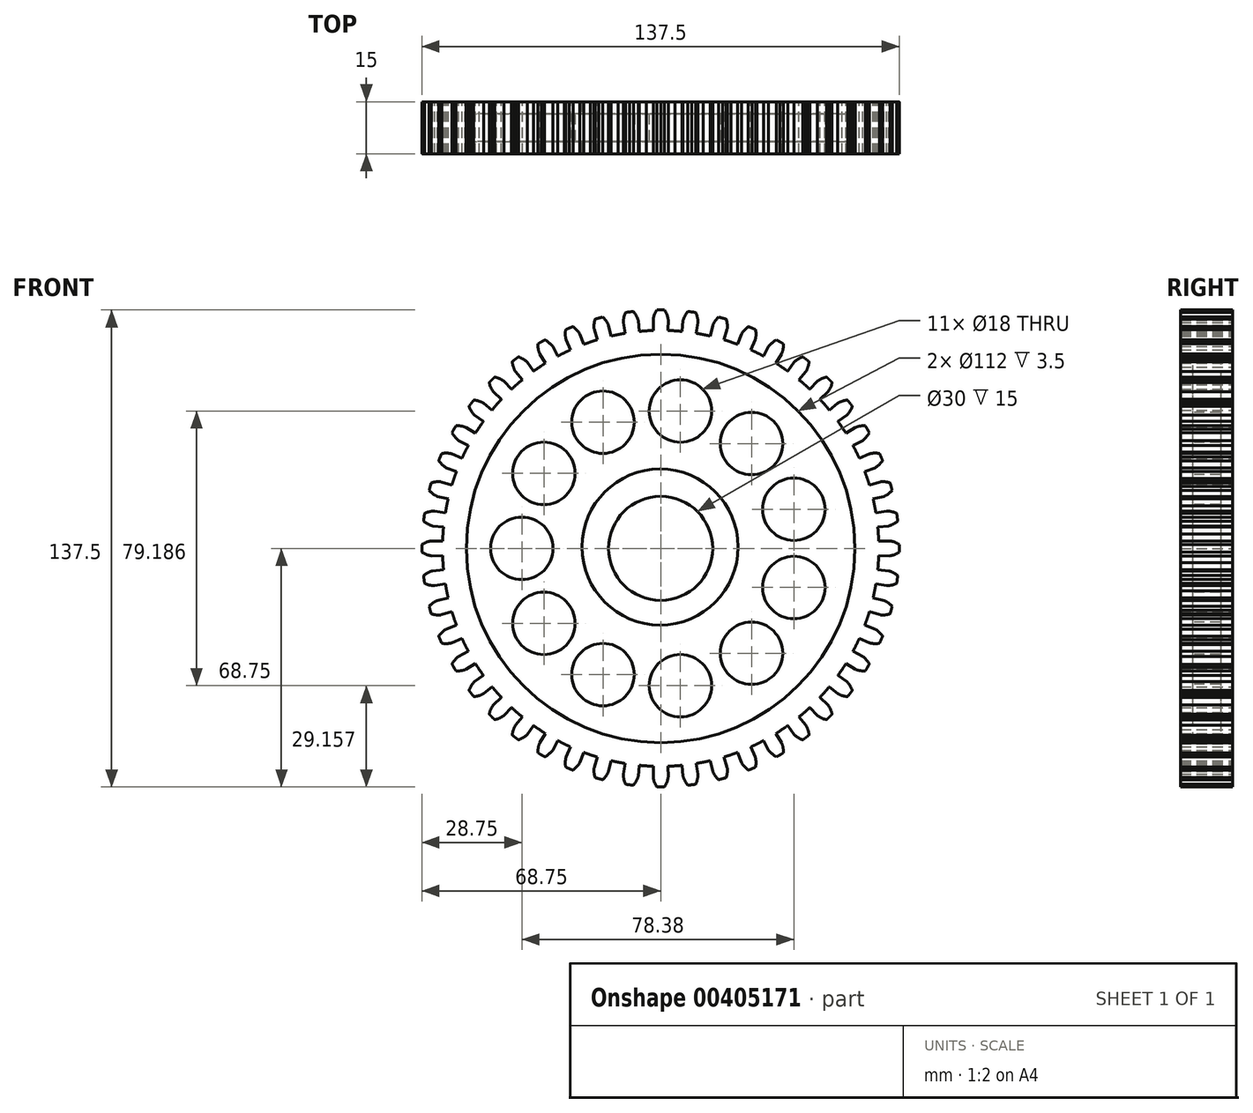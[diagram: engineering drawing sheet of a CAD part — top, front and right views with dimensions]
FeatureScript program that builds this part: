
annotation { "Feature Type Name" : "Feature", "Feature Type Description" : "" }
export const myFeature = defineFeature(function(context is Context, id is Id, definition is map)
    precondition{}
    {
        {
            var Q0;
            Q0=qCreatedBy(makeId("Front.planeOp"),FACE);
            var sketch = newSketch(context, id + "F0", { "sketchPlane" : qUnion([Q0])});
            skArc(sketch, "E0", {"start": v(68.74, -1.12) * mm, "mid": v(68.75, 0) * mm, "end": v(68.74, 1.12) * mm});
            skArc(sketch, "E1", {"start": v(62.82, 2.06) * mm, "mid": v(-62.85, 0) * mm, "end": v(62.82, -2.06) * mm});
            skLineSegment(sketch, "E2", {"start": v(62.82, 2.06) * mm, "end": v(65.96, 2.16) * mm});
            skLineSegment(sketch, "E3", {"start": v(62.82, 1.03) * mm, "end": v(62.84, 1.03) * mm});
            skArc(sketch, "E4", {"start": v(68.74, 1.12) * mm, "mid": v(67.41, 1.8) * mm, "end": v(65.96, 2.16) * mm});
            skLineSegment(sketch, "E5", {"start": v(65.96, 2.16) * mm, "end": v(62.82, 2.06) * mm});
            skArc(sketch, "E6", {"start": v(62.82, 2.06) * mm, "mid": v(62.78, 3.08) * mm, "end": v(62.72, 4.11) * mm});
            skArc(sketch, "E7", {"start": v(68.75, 0) * mm, "mid": v(68.75, 0.56) * mm, "end": v(68.74, 1.12) * mm});
            skLineSegment(sketch, "E8", {"start": v(62.78, 0) * mm, "end": v(62.85, 0) * mm});
            skArc(sketch, "E9.MirrorCS", {"start": v(68.75, 0) * mm, "mid": v(68.75, -0.56) * mm, "end": v(68.74, -1.12) * mm});
            skLineSegment(sketch, "E10.MirrorCS", {"start": v(65.96, -2.16) * mm, "end": v(62.82, -2.06) * mm});
            skArc(sketch, "E11.MirrorCS", {"start": v(68.74, -1.12) * mm, "mid": v(67.41, -1.8) * mm, "end": v(65.96, -2.16) * mm});
            skArc(sketch, "E12.MirrorCS", {"start": v(62.82, -2.06) * mm, "mid": v(62.78, -3.08) * mm, "end": v(62.72, -4.11) * mm});
            skPoint(sketch, "E13.trimOffspring.end.orphan", {"position": v(73.8, 0) * mm});
            skArc(sketch, "E14.1.0", {"start": v(62.01, 10.24) * mm, "mid": v(61.84, 11.25) * mm, "end": v(61.64, 12.26) * mm});
            skLineSegment(sketch, "E14.1.1", {"start": v(65.12, 10.75) * mm, "end": v(62.01, 10.24) * mm});
            skArc(sketch, "E14.1.2", {"start": v(68, 10.09) * mm, "mid": v(66.6, 10.59) * mm, "end": v(65.12, 10.75) * mm});
            skArc(sketch, "E14.1.3", {"start": v(68.16, 8.97) * mm, "mid": v(68.09, 9.53) * mm, "end": v(68, 10.09) * mm});
            skArc(sketch, "E14.1.4", {"start": v(68.16, 8.97) * mm, "mid": v(68.24, 8.42) * mm, "end": v(68.3, 7.86) * mm});
            skArc(sketch, "E14.1.5", {"start": v(68.3, 7.86) * mm, "mid": v(67.07, 7.01) * mm, "end": v(65.68, 6.47) * mm});
            skLineSegment(sketch, "E14.1.6", {"start": v(65.68, 6.47) * mm, "end": v(62.55, 6.16) * mm});
            skArc(sketch, "E14.1.7", {"start": v(62.55, 6.16) * mm, "mid": v(62.65, 5.14) * mm, "end": v(62.72, 4.11) * mm});
            skArc(sketch, "E14.2.0", {"start": v(60.14, 18.24) * mm, "mid": v(59.85, 19.23) * mm, "end": v(59.51, 20.2) * mm});
            skLineSegment(sketch, "E14.2.1", {"start": v(63.16, 19.16) * mm, "end": v(60.14, 18.24) * mm});
            skArc(sketch, "E14.2.2", {"start": v(66.1, 18.88) * mm, "mid": v(64.65, 19.19) * mm, "end": v(63.16, 19.16) * mm});
            skArc(sketch, "E14.2.3", {"start": v(66.4, 17.8) * mm, "mid": v(66.26, 18.34) * mm, "end": v(66.1, 18.88) * mm});
            skArc(sketch, "E14.2.4", {"start": v(66.4, 17.8) * mm, "mid": v(66.55, 17.25) * mm, "end": v(66.69, 16.7) * mm});
            skArc(sketch, "E14.2.5", {"start": v(66.69, 16.7) * mm, "mid": v(65.58, 15.7) * mm, "end": v(64.28, 14.99) * mm});
            skLineSegment(sketch, "E14.2.6", {"start": v(64.28, 14.99) * mm, "end": v(61.2, 14.27) * mm});
            skArc(sketch, "E14.2.7", {"start": v(61.2, 14.27) * mm, "mid": v(61.44, 13.27) * mm, "end": v(61.64, 12.26) * mm});
            skArc(sketch, "E14.3.0", {"start": v(57.25, 25.94) * mm, "mid": v(56.82, 26.88) * mm, "end": v(56.37, 27.8) * mm});
            skLineSegment(sketch, "E14.3.1", {"start": v(60.12, 27.24) * mm, "end": v(57.25, 25.94) * mm});
            skArc(sketch, "E14.3.2", {"start": v(63.08, 27.34) * mm, "mid": v(61.6, 27.46) * mm, "end": v(60.12, 27.24) * mm});
            skArc(sketch, "E14.3.3", {"start": v(63.52, 26.3) * mm, "mid": v(63.3, 26.83) * mm, "end": v(63.08, 27.34) * mm});
            skArc(sketch, "E14.3.4", {"start": v(63.52, 26.3) * mm, "mid": v(63.73, 25.8) * mm, "end": v(63.94, 25.27) * mm});
            skArc(sketch, "E14.3.5", {"start": v(63.94, 25.27) * mm, "mid": v(62.97, 24.13) * mm, "end": v(61.77, 23.25) * mm});
            skLineSegment(sketch, "E14.3.6", {"start": v(61.77, 23.25) * mm, "end": v(58.82, 22.14) * mm});
            skArc(sketch, "E14.3.7", {"start": v(58.82, 22.14) * mm, "mid": v(59.18, 21.18) * mm, "end": v(59.51, 20.2) * mm});
            skArc(sketch, "E14.4.0", {"start": v(53.37, 33.19) * mm, "mid": v(52.83, 34.06) * mm, "end": v(52.26, 34.92) * mm});
            skLineSegment(sketch, "E14.4.1", {"start": v(56.05, 34.85) * mm, "end": v(53.37, 33.19) * mm});
            skArc(sketch, "E14.4.2", {"start": v(58.97, 35.34) * mm, "mid": v(57.48, 35.27) * mm, "end": v(56.05, 34.85) * mm});
            skArc(sketch, "E14.4.3", {"start": v(59.54, 34.37) * mm, "mid": v(59.26, 34.86) * mm, "end": v(58.97, 35.34) * mm});
            skArc(sketch, "E14.4.4", {"start": v(59.54, 34.37) * mm, "mid": v(59.82, 33.89) * mm, "end": v(60.1, 33.4) * mm});
            skArc(sketch, "E14.4.5", {"start": v(60.1, 33.4) * mm, "mid": v(59.28, 32.14) * mm, "end": v(58.2, 31.11) * mm});
            skLineSegment(sketch, "E14.4.6", {"start": v(58.2, 31.11) * mm, "end": v(55.43, 29.63) * mm});
            skArc(sketch, "E14.4.7", {"start": v(55.43, 29.63) * mm, "mid": v(55.91, 28.72) * mm, "end": v(56.37, 27.8) * mm});
            skArc(sketch, "E14.5.0", {"start": v(48.58, 39.87) * mm, "mid": v(47.93, 40.67) * mm, "end": v(47.25, 41.44) * mm});
            skLineSegment(sketch, "E14.5.1", {"start": v(51.02, 41.87) * mm, "end": v(48.58, 39.87) * mm});
            skArc(sketch, "E14.5.2", {"start": v(53.85, 42.74) * mm, "mid": v(52.38, 42.47) * mm, "end": v(51.02, 41.87) * mm});
            skArc(sketch, "E14.5.3", {"start": v(54.54, 41.85) * mm, "mid": v(54.2, 42.3) * mm, "end": v(53.85, 42.74) * mm});
            skArc(sketch, "E14.5.4", {"start": v(54.54, 41.85) * mm, "mid": v(54.89, 41.4) * mm, "end": v(55.22, 40.95) * mm});
            skArc(sketch, "E14.5.5", {"start": v(55.22, 40.95) * mm, "mid": v(54.58, 39.6) * mm, "end": v(53.65, 38.44) * mm});
            skLineSegment(sketch, "E14.5.6", {"start": v(53.65, 38.44) * mm, "end": v(51.09, 36.6) * mm});
            skArc(sketch, "E14.5.7", {"start": v(51.09, 36.6) * mm, "mid": v(51.69, 35.77) * mm, "end": v(52.26, 34.92) * mm});
            skArc(sketch, "E14.6.0", {"start": v(42.96, 45.87) * mm, "mid": v(42.21, 46.58) * mm, "end": v(41.44, 47.25) * mm});
            skLineSegment(sketch, "E14.6.1", {"start": v(45.12, 48.17) * mm, "end": v(42.96, 45.87) * mm});
            skArc(sketch, "E14.6.2", {"start": v(47.81, 49.4) * mm, "mid": v(46.4, 48.94) * mm, "end": v(45.12, 48.17) * mm});
            skArc(sketch, "E14.6.3", {"start": v(48.61, 48.61) * mm, "mid": v(48.22, 49.01) * mm, "end": v(47.81, 49.4) * mm});
            skArc(sketch, "E14.6.4", {"start": v(48.61, 48.61) * mm, "mid": v(49.01, 48.22) * mm, "end": v(49.4, 47.81) * mm});
            skArc(sketch, "E14.6.5", {"start": v(49.4, 47.81) * mm, "mid": v(48.94, 46.4) * mm, "end": v(48.17, 45.12) * mm});
            skLineSegment(sketch, "E14.6.6", {"start": v(48.17, 45.12) * mm, "end": v(45.87, 42.96) * mm});
            skArc(sketch, "E14.6.7", {"start": v(45.87, 42.96) * mm, "mid": v(46.58, 42.21) * mm, "end": v(47.25, 41.44) * mm});
            skArc(sketch, "E14.7.0", {"start": v(36.6, 51.09) * mm, "mid": v(35.77, 51.69) * mm, "end": v(34.92, 52.26) * mm});
            skLineSegment(sketch, "E14.7.1", {"start": v(38.44, 53.65) * mm, "end": v(36.6, 51.09) * mm});
            skArc(sketch, "E14.7.2", {"start": v(40.95, 55.22) * mm, "mid": v(39.6, 54.58) * mm, "end": v(38.44, 53.65) * mm});
            skArc(sketch, "E14.7.3", {"start": v(41.85, 54.54) * mm, "mid": v(41.4, 54.89) * mm, "end": v(40.95, 55.22) * mm});
            skArc(sketch, "E14.7.4", {"start": v(41.85, 54.54) * mm, "mid": v(42.3, 54.2) * mm, "end": v(42.74, 53.85) * mm});
            skArc(sketch, "E14.7.5", {"start": v(42.74, 53.85) * mm, "mid": v(42.47, 52.38) * mm, "end": v(41.87, 51.02) * mm});
            skLineSegment(sketch, "E14.7.6", {"start": v(41.87, 51.02) * mm, "end": v(39.87, 48.58) * mm});
            skArc(sketch, "E14.7.7", {"start": v(39.87, 48.58) * mm, "mid": v(40.67, 47.93) * mm, "end": v(41.44, 47.25) * mm});
            skArc(sketch, "E14.8.0", {"start": v(29.63, 55.43) * mm, "mid": v(28.72, 55.91) * mm, "end": v(27.8, 56.37) * mm});
            skLineSegment(sketch, "E14.8.1", {"start": v(31.11, 58.2) * mm, "end": v(29.63, 55.43) * mm});
            skArc(sketch, "E14.8.2", {"start": v(33.4, 60.1) * mm, "mid": v(32.14, 59.28) * mm, "end": v(31.11, 58.2) * mm});
            skArc(sketch, "E14.8.3", {"start": v(34.37, 59.54) * mm, "mid": v(33.89, 59.82) * mm, "end": v(33.4, 60.1) * mm});
            skArc(sketch, "E14.8.4", {"start": v(34.37, 59.54) * mm, "mid": v(34.86, 59.26) * mm, "end": v(35.34, 58.97) * mm});
            skArc(sketch, "E14.8.5", {"start": v(35.34, 58.97) * mm, "mid": v(35.27, 57.48) * mm, "end": v(34.85, 56.05) * mm});
            skLineSegment(sketch, "E14.8.6", {"start": v(34.85, 56.05) * mm, "end": v(33.19, 53.37) * mm});
            skArc(sketch, "E14.8.7", {"start": v(33.19, 53.37) * mm, "mid": v(34.06, 52.83) * mm, "end": v(34.92, 52.26) * mm});
            skArc(sketch, "E14.9.0", {"start": v(22.14, 58.82) * mm, "mid": v(21.18, 59.18) * mm, "end": v(20.2, 59.51) * mm});
            skLineSegment(sketch, "E14.9.1", {"start": v(23.25, 61.77) * mm, "end": v(22.14, 58.82) * mm});
            skArc(sketch, "E14.9.2", {"start": v(25.27, 63.94) * mm, "mid": v(24.13, 62.97) * mm, "end": v(23.25, 61.77) * mm});
            skArc(sketch, "E14.9.3", {"start": v(26.3, 63.52) * mm, "mid": v(25.8, 63.73) * mm, "end": v(25.27, 63.94) * mm});
            skArc(sketch, "E14.9.4", {"start": v(26.3, 63.52) * mm, "mid": v(26.83, 63.3) * mm, "end": v(27.34, 63.08) * mm});
            skArc(sketch, "E14.9.5", {"start": v(27.34, 63.08) * mm, "mid": v(27.46, 61.6) * mm, "end": v(27.24, 60.12) * mm});
            skLineSegment(sketch, "E14.9.6", {"start": v(27.24, 60.12) * mm, "end": v(25.94, 57.25) * mm});
            skArc(sketch, "E14.9.7", {"start": v(25.94, 57.25) * mm, "mid": v(26.88, 56.82) * mm, "end": v(27.8, 56.37) * mm});
            skArc(sketch, "E14.10.0", {"start": v(14.27, 61.2) * mm, "mid": v(13.27, 61.44) * mm, "end": v(12.26, 61.64) * mm});
            skLineSegment(sketch, "E14.10.1", {"start": v(14.99, 64.28) * mm, "end": v(14.27, 61.2) * mm});
            skArc(sketch, "E14.10.2", {"start": v(16.7, 66.69) * mm, "mid": v(15.7, 65.58) * mm, "end": v(14.99, 64.28) * mm});
            skArc(sketch, "E14.10.3", {"start": v(17.8, 66.4) * mm, "mid": v(17.25, 66.55) * mm, "end": v(16.7, 66.69) * mm});
            skArc(sketch, "E14.10.4", {"start": v(17.8, 66.4) * mm, "mid": v(18.34, 66.26) * mm, "end": v(18.88, 66.1) * mm});
            skArc(sketch, "E14.10.5", {"start": v(18.88, 66.1) * mm, "mid": v(19.19, 64.65) * mm, "end": v(19.16, 63.16) * mm});
            skLineSegment(sketch, "E14.10.6", {"start": v(19.16, 63.16) * mm, "end": v(18.24, 60.14) * mm});
            skArc(sketch, "E14.10.7", {"start": v(18.24, 60.14) * mm, "mid": v(19.23, 59.85) * mm, "end": v(20.2, 59.51) * mm});
            skArc(sketch, "E14.11.0", {"start": v(6.16, 62.55) * mm, "mid": v(5.14, 62.65) * mm, "end": v(4.11, 62.72) * mm});
            skLineSegment(sketch, "E14.11.1", {"start": v(6.47, 65.68) * mm, "end": v(6.16, 62.55) * mm});
            skArc(sketch, "E14.11.2", {"start": v(7.86, 68.3) * mm, "mid": v(7.01, 67.07) * mm, "end": v(6.47, 65.68) * mm});
            skArc(sketch, "E14.11.3", {"start": v(8.97, 68.16) * mm, "mid": v(8.42, 68.24) * mm, "end": v(7.86, 68.3) * mm});
            skArc(sketch, "E14.11.4", {"start": v(8.97, 68.16) * mm, "mid": v(9.53, 68.09) * mm, "end": v(10.09, 68) * mm});
            skArc(sketch, "E14.11.5", {"start": v(10.09, 68) * mm, "mid": v(10.59, 66.6) * mm, "end": v(10.75, 65.12) * mm});
            skLineSegment(sketch, "E14.11.6", {"start": v(10.75, 65.12) * mm, "end": v(10.24, 62.01) * mm});
            skArc(sketch, "E14.11.7", {"start": v(10.24, 62.01) * mm, "mid": v(11.25, 61.84) * mm, "end": v(12.26, 61.64) * mm});
            skArc(sketch, "E14.12.0", {"start": v(-2.06, 62.82) * mm, "mid": v(-3.08, 62.78) * mm, "end": v(-4.11, 62.72) * mm});
            skLineSegment(sketch, "E14.12.1", {"start": v(-2.16, 65.96) * mm, "end": v(-2.06, 62.82) * mm});
            skArc(sketch, "E14.12.2", {"start": v(-1.12, 68.74) * mm, "mid": v(-1.8, 67.41) * mm, "end": v(-2.16, 65.96) * mm});
            skArc(sketch, "E14.12.3", {"start": v(0, 68.75) * mm, "mid": v(-0.56, 68.75) * mm, "end": v(-1.12, 68.74) * mm});
            skArc(sketch, "E14.12.4", {"start": v(0, 68.75) * mm, "mid": v(0.56, 68.75) * mm, "end": v(1.12, 68.74) * mm});
            skArc(sketch, "E14.12.5", {"start": v(1.12, 68.74) * mm, "mid": v(1.8, 67.41) * mm, "end": v(2.16, 65.96) * mm});
            skLineSegment(sketch, "E14.12.6", {"start": v(2.16, 65.96) * mm, "end": v(2.06, 62.82) * mm});
            skArc(sketch, "E14.12.7", {"start": v(2.06, 62.82) * mm, "mid": v(3.08, 62.78) * mm, "end": v(4.11, 62.72) * mm});
            skArc(sketch, "E14.13.0", {"start": v(-10.24, 62.01) * mm, "mid": v(-11.25, 61.84) * mm, "end": v(-12.26, 61.64) * mm});
            skLineSegment(sketch, "E14.13.1", {"start": v(-10.75, 65.12) * mm, "end": v(-10.24, 62.01) * mm});
            skArc(sketch, "E14.13.2", {"start": v(-10.09, 68) * mm, "mid": v(-10.59, 66.6) * mm, "end": v(-10.75, 65.12) * mm});
            skArc(sketch, "E14.13.3", {"start": v(-8.97, 68.16) * mm, "mid": v(-9.53, 68.09) * mm, "end": v(-10.09, 68) * mm});
            skArc(sketch, "E14.13.4", {"start": v(-8.97, 68.16) * mm, "mid": v(-8.42, 68.24) * mm, "end": v(-7.86, 68.3) * mm});
            skArc(sketch, "E14.13.5", {"start": v(-7.86, 68.3) * mm, "mid": v(-7.01, 67.07) * mm, "end": v(-6.47, 65.68) * mm});
            skLineSegment(sketch, "E14.13.6", {"start": v(-6.47, 65.68) * mm, "end": v(-6.16, 62.55) * mm});
            skArc(sketch, "E14.13.7", {"start": v(-6.16, 62.55) * mm, "mid": v(-5.14, 62.65) * mm, "end": v(-4.11, 62.72) * mm});
            skArc(sketch, "E14.14.0", {"start": v(-18.24, 60.14) * mm, "mid": v(-19.23, 59.85) * mm, "end": v(-20.2, 59.51) * mm});
            skLineSegment(sketch, "E14.14.1", {"start": v(-19.16, 63.16) * mm, "end": v(-18.24, 60.14) * mm});
            skArc(sketch, "E14.14.2", {"start": v(-18.88, 66.1) * mm, "mid": v(-19.19, 64.65) * mm, "end": v(-19.16, 63.16) * mm});
            skArc(sketch, "E14.14.3", {"start": v(-17.8, 66.4) * mm, "mid": v(-18.34, 66.26) * mm, "end": v(-18.88, 66.1) * mm});
            skArc(sketch, "E14.14.4", {"start": v(-17.8, 66.4) * mm, "mid": v(-17.25, 66.55) * mm, "end": v(-16.7, 66.69) * mm});
            skArc(sketch, "E14.14.5", {"start": v(-16.7, 66.69) * mm, "mid": v(-15.7, 65.58) * mm, "end": v(-14.99, 64.28) * mm});
            skLineSegment(sketch, "E14.14.6", {"start": v(-14.99, 64.28) * mm, "end": v(-14.27, 61.2) * mm});
            skArc(sketch, "E14.14.7", {"start": v(-14.27, 61.2) * mm, "mid": v(-13.27, 61.44) * mm, "end": v(-12.26, 61.64) * mm});
            skArc(sketch, "E14.15.0", {"start": v(-25.94, 57.25) * mm, "mid": v(-26.88, 56.82) * mm, "end": v(-27.8, 56.37) * mm});
            skLineSegment(sketch, "E14.15.1", {"start": v(-27.24, 60.12) * mm, "end": v(-25.94, 57.25) * mm});
            skArc(sketch, "E14.15.2", {"start": v(-27.34, 63.08) * mm, "mid": v(-27.46, 61.6) * mm, "end": v(-27.24, 60.12) * mm});
            skArc(sketch, "E14.15.3", {"start": v(-26.3, 63.52) * mm, "mid": v(-26.83, 63.3) * mm, "end": v(-27.34, 63.08) * mm});
            skArc(sketch, "E14.15.4", {"start": v(-26.3, 63.52) * mm, "mid": v(-25.8, 63.73) * mm, "end": v(-25.27, 63.94) * mm});
            skArc(sketch, "E14.15.5", {"start": v(-25.27, 63.94) * mm, "mid": v(-24.13, 62.97) * mm, "end": v(-23.25, 61.77) * mm});
            skLineSegment(sketch, "E14.15.6", {"start": v(-23.25, 61.77) * mm, "end": v(-22.14, 58.82) * mm});
            skArc(sketch, "E14.15.7", {"start": v(-22.14, 58.82) * mm, "mid": v(-21.18, 59.18) * mm, "end": v(-20.2, 59.51) * mm});
            skArc(sketch, "E14.16.0", {"start": v(-33.19, 53.37) * mm, "mid": v(-34.06, 52.83) * mm, "end": v(-34.92, 52.26) * mm});
            skLineSegment(sketch, "E14.16.1", {"start": v(-34.85, 56.05) * mm, "end": v(-33.19, 53.37) * mm});
            skArc(sketch, "E14.16.2", {"start": v(-35.34, 58.97) * mm, "mid": v(-35.27, 57.48) * mm, "end": v(-34.85, 56.05) * mm});
            skArc(sketch, "E14.16.3", {"start": v(-34.37, 59.54) * mm, "mid": v(-34.86, 59.26) * mm, "end": v(-35.34, 58.97) * mm});
            skArc(sketch, "E14.16.4", {"start": v(-34.37, 59.54) * mm, "mid": v(-33.89, 59.82) * mm, "end": v(-33.4, 60.1) * mm});
            skArc(sketch, "E14.16.5", {"start": v(-33.4, 60.1) * mm, "mid": v(-32.14, 59.28) * mm, "end": v(-31.11, 58.2) * mm});
            skLineSegment(sketch, "E14.16.6", {"start": v(-31.11, 58.2) * mm, "end": v(-29.63, 55.43) * mm});
            skArc(sketch, "E14.16.7", {"start": v(-29.63, 55.43) * mm, "mid": v(-28.72, 55.91) * mm, "end": v(-27.8, 56.37) * mm});
            skArc(sketch, "E14.17.0", {"start": v(-39.87, 48.58) * mm, "mid": v(-40.67, 47.93) * mm, "end": v(-41.44, 47.25) * mm});
            skLineSegment(sketch, "E14.17.1", {"start": v(-41.87, 51.02) * mm, "end": v(-39.87, 48.58) * mm});
            skArc(sketch, "E14.17.2", {"start": v(-42.74, 53.85) * mm, "mid": v(-42.47, 52.38) * mm, "end": v(-41.87, 51.02) * mm});
            skArc(sketch, "E14.17.3", {"start": v(-41.85, 54.54) * mm, "mid": v(-42.3, 54.2) * mm, "end": v(-42.74, 53.85) * mm});
            skArc(sketch, "E14.17.4", {"start": v(-41.85, 54.54) * mm, "mid": v(-41.4, 54.89) * mm, "end": v(-40.95, 55.22) * mm});
            skArc(sketch, "E14.17.5", {"start": v(-40.95, 55.22) * mm, "mid": v(-39.6, 54.58) * mm, "end": v(-38.44, 53.65) * mm});
            skLineSegment(sketch, "E14.17.6", {"start": v(-38.44, 53.65) * mm, "end": v(-36.6, 51.09) * mm});
            skArc(sketch, "E14.17.7", {"start": v(-36.6, 51.09) * mm, "mid": v(-35.77, 51.69) * mm, "end": v(-34.92, 52.26) * mm});
            skArc(sketch, "E14.18.0", {"start": v(-45.87, 42.96) * mm, "mid": v(-46.58, 42.21) * mm, "end": v(-47.25, 41.44) * mm});
            skLineSegment(sketch, "E14.18.1", {"start": v(-48.17, 45.12) * mm, "end": v(-45.87, 42.96) * mm});
            skArc(sketch, "E14.18.2", {"start": v(-49.4, 47.81) * mm, "mid": v(-48.94, 46.4) * mm, "end": v(-48.17, 45.12) * mm});
            skArc(sketch, "E14.18.3", {"start": v(-48.61, 48.61) * mm, "mid": v(-49.01, 48.22) * mm, "end": v(-49.4, 47.81) * mm});
            skArc(sketch, "E14.18.4", {"start": v(-48.61, 48.61) * mm, "mid": v(-48.22, 49.01) * mm, "end": v(-47.81, 49.4) * mm});
            skArc(sketch, "E14.18.5", {"start": v(-47.81, 49.4) * mm, "mid": v(-46.4, 48.94) * mm, "end": v(-45.12, 48.17) * mm});
            skLineSegment(sketch, "E14.18.6", {"start": v(-45.12, 48.17) * mm, "end": v(-42.96, 45.87) * mm});
            skArc(sketch, "E14.18.7", {"start": v(-42.96, 45.87) * mm, "mid": v(-42.21, 46.58) * mm, "end": v(-41.44, 47.25) * mm});
            skArc(sketch, "E14.19.0", {"start": v(-51.09, 36.6) * mm, "mid": v(-51.69, 35.77) * mm, "end": v(-52.26, 34.92) * mm});
            skLineSegment(sketch, "E14.19.1", {"start": v(-53.65, 38.44) * mm, "end": v(-51.09, 36.6) * mm});
            skArc(sketch, "E14.19.2", {"start": v(-55.22, 40.95) * mm, "mid": v(-54.58, 39.6) * mm, "end": v(-53.65, 38.44) * mm});
            skArc(sketch, "E14.19.3", {"start": v(-54.54, 41.85) * mm, "mid": v(-54.89, 41.4) * mm, "end": v(-55.22, 40.95) * mm});
            skArc(sketch, "E14.19.4", {"start": v(-54.54, 41.85) * mm, "mid": v(-54.2, 42.3) * mm, "end": v(-53.85, 42.74) * mm});
            skArc(sketch, "E14.19.5", {"start": v(-53.85, 42.74) * mm, "mid": v(-52.38, 42.47) * mm, "end": v(-51.02, 41.87) * mm});
            skLineSegment(sketch, "E14.19.6", {"start": v(-51.02, 41.87) * mm, "end": v(-48.58, 39.87) * mm});
            skArc(sketch, "E14.19.7", {"start": v(-48.58, 39.87) * mm, "mid": v(-47.93, 40.67) * mm, "end": v(-47.25, 41.44) * mm});
            skArc(sketch, "E14.20.0", {"start": v(-55.43, 29.63) * mm, "mid": v(-55.91, 28.72) * mm, "end": v(-56.37, 27.8) * mm});
            skLineSegment(sketch, "E14.20.1", {"start": v(-58.2, 31.11) * mm, "end": v(-55.43, 29.63) * mm});
            skArc(sketch, "E14.20.2", {"start": v(-60.1, 33.4) * mm, "mid": v(-59.28, 32.14) * mm, "end": v(-58.2, 31.11) * mm});
            skArc(sketch, "E14.20.3", {"start": v(-59.54, 34.37) * mm, "mid": v(-59.82, 33.89) * mm, "end": v(-60.1, 33.4) * mm});
            skArc(sketch, "E14.20.4", {"start": v(-59.54, 34.37) * mm, "mid": v(-59.26, 34.86) * mm, "end": v(-58.97, 35.34) * mm});
            skArc(sketch, "E14.20.5", {"start": v(-58.97, 35.34) * mm, "mid": v(-57.48, 35.27) * mm, "end": v(-56.05, 34.85) * mm});
            skLineSegment(sketch, "E14.20.6", {"start": v(-56.05, 34.85) * mm, "end": v(-53.37, 33.19) * mm});
            skArc(sketch, "E14.20.7", {"start": v(-53.37, 33.19) * mm, "mid": v(-52.83, 34.06) * mm, "end": v(-52.26, 34.92) * mm});
            skArc(sketch, "E14.21.0", {"start": v(-58.82, 22.14) * mm, "mid": v(-59.18, 21.18) * mm, "end": v(-59.51, 20.2) * mm});
            skLineSegment(sketch, "E14.21.1", {"start": v(-61.77, 23.25) * mm, "end": v(-58.82, 22.14) * mm});
            skArc(sketch, "E14.21.2", {"start": v(-63.94, 25.27) * mm, "mid": v(-62.97, 24.13) * mm, "end": v(-61.77, 23.25) * mm});
            skArc(sketch, "E14.21.3", {"start": v(-63.52, 26.3) * mm, "mid": v(-63.73, 25.8) * mm, "end": v(-63.94, 25.27) * mm});
            skArc(sketch, "E14.21.4", {"start": v(-63.52, 26.3) * mm, "mid": v(-63.3, 26.83) * mm, "end": v(-63.08, 27.34) * mm});
            skArc(sketch, "E14.21.5", {"start": v(-63.08, 27.34) * mm, "mid": v(-61.6, 27.46) * mm, "end": v(-60.12, 27.24) * mm});
            skLineSegment(sketch, "E14.21.6", {"start": v(-60.12, 27.24) * mm, "end": v(-57.25, 25.94) * mm});
            skArc(sketch, "E14.21.7", {"start": v(-57.25, 25.94) * mm, "mid": v(-56.82, 26.88) * mm, "end": v(-56.37, 27.8) * mm});
            skArc(sketch, "E14.22.0", {"start": v(-61.2, 14.27) * mm, "mid": v(-61.44, 13.27) * mm, "end": v(-61.64, 12.26) * mm});
            skLineSegment(sketch, "E14.22.1", {"start": v(-64.28, 14.99) * mm, "end": v(-61.2, 14.27) * mm});
            skArc(sketch, "E14.22.2", {"start": v(-66.69, 16.7) * mm, "mid": v(-65.58, 15.7) * mm, "end": v(-64.28, 14.99) * mm});
            skArc(sketch, "E14.22.3", {"start": v(-66.4, 17.8) * mm, "mid": v(-66.55, 17.25) * mm, "end": v(-66.69, 16.7) * mm});
            skArc(sketch, "E14.22.4", {"start": v(-66.4, 17.8) * mm, "mid": v(-66.26, 18.34) * mm, "end": v(-66.1, 18.88) * mm});
            skArc(sketch, "E14.22.5", {"start": v(-66.1, 18.88) * mm, "mid": v(-64.65, 19.19) * mm, "end": v(-63.16, 19.16) * mm});
            skLineSegment(sketch, "E14.22.6", {"start": v(-63.16, 19.16) * mm, "end": v(-60.14, 18.24) * mm});
            skArc(sketch, "E14.22.7", {"start": v(-60.14, 18.24) * mm, "mid": v(-59.85, 19.23) * mm, "end": v(-59.51, 20.2) * mm});
            skArc(sketch, "E14.23.0", {"start": v(-62.55, 6.16) * mm, "mid": v(-62.65, 5.14) * mm, "end": v(-62.72, 4.11) * mm});
            skLineSegment(sketch, "E14.23.1", {"start": v(-65.68, 6.47) * mm, "end": v(-62.55, 6.16) * mm});
            skArc(sketch, "E14.23.2", {"start": v(-68.3, 7.86) * mm, "mid": v(-67.07, 7.01) * mm, "end": v(-65.68, 6.47) * mm});
            skArc(sketch, "E14.23.3", {"start": v(-68.16, 8.97) * mm, "mid": v(-68.24, 8.42) * mm, "end": v(-68.3, 7.86) * mm});
            skArc(sketch, "E14.23.4", {"start": v(-68.16, 8.97) * mm, "mid": v(-68.09, 9.53) * mm, "end": v(-68, 10.09) * mm});
            skArc(sketch, "E14.23.5", {"start": v(-68, 10.09) * mm, "mid": v(-66.6, 10.59) * mm, "end": v(-65.12, 10.75) * mm});
            skLineSegment(sketch, "E14.23.6", {"start": v(-65.12, 10.75) * mm, "end": v(-62.01, 10.24) * mm});
            skArc(sketch, "E14.23.7", {"start": v(-62.01, 10.24) * mm, "mid": v(-61.84, 11.25) * mm, "end": v(-61.64, 12.26) * mm});
            skArc(sketch, "E14.24.0", {"start": v(-62.82, -2.06) * mm, "mid": v(-62.78, -3.08) * mm, "end": v(-62.72, -4.11) * mm});
            skLineSegment(sketch, "E14.24.1", {"start": v(-65.96, -2.16) * mm, "end": v(-62.82, -2.06) * mm});
            skArc(sketch, "E14.24.2", {"start": v(-68.74, -1.12) * mm, "mid": v(-67.41, -1.8) * mm, "end": v(-65.96, -2.16) * mm});
            skArc(sketch, "E14.24.3", {"start": v(-68.75, 0) * mm, "mid": v(-68.75, -0.56) * mm, "end": v(-68.74, -1.12) * mm});
            skArc(sketch, "E14.24.4", {"start": v(-68.75, 0) * mm, "mid": v(-68.75, 0.56) * mm, "end": v(-68.74, 1.12) * mm});
            skArc(sketch, "E14.24.5", {"start": v(-68.74, 1.12) * mm, "mid": v(-67.41, 1.8) * mm, "end": v(-65.96, 2.16) * mm});
            skLineSegment(sketch, "E14.24.6", {"start": v(-65.96, 2.16) * mm, "end": v(-62.82, 2.06) * mm});
            skArc(sketch, "E14.24.7", {"start": v(-62.82, 2.06) * mm, "mid": v(-62.78, 3.08) * mm, "end": v(-62.72, 4.11) * mm});
            skArc(sketch, "E14.25.0", {"start": v(-62.01, -10.24) * mm, "mid": v(-61.84, -11.25) * mm, "end": v(-61.64, -12.26) * mm});
            skLineSegment(sketch, "E14.25.1", {"start": v(-65.12, -10.75) * mm, "end": v(-62.01, -10.24) * mm});
            skArc(sketch, "E14.25.2", {"start": v(-68, -10.09) * mm, "mid": v(-66.6, -10.59) * mm, "end": v(-65.12, -10.75) * mm});
            skArc(sketch, "E14.25.3", {"start": v(-68.16, -8.97) * mm, "mid": v(-68.09, -9.53) * mm, "end": v(-68, -10.09) * mm});
            skArc(sketch, "E14.25.4", {"start": v(-68.16, -8.97) * mm, "mid": v(-68.24, -8.42) * mm, "end": v(-68.3, -7.86) * mm});
            skArc(sketch, "E14.25.5", {"start": v(-68.3, -7.86) * mm, "mid": v(-67.07, -7.01) * mm, "end": v(-65.68, -6.47) * mm});
            skLineSegment(sketch, "E14.25.6", {"start": v(-65.68, -6.47) * mm, "end": v(-62.55, -6.16) * mm});
            skArc(sketch, "E14.25.7", {"start": v(-62.55, -6.16) * mm, "mid": v(-62.65, -5.14) * mm, "end": v(-62.72, -4.11) * mm});
            skArc(sketch, "E14.26.0", {"start": v(-60.14, -18.24) * mm, "mid": v(-59.85, -19.23) * mm, "end": v(-59.51, -20.2) * mm});
            skLineSegment(sketch, "E14.26.1", {"start": v(-63.16, -19.16) * mm, "end": v(-60.14, -18.24) * mm});
            skArc(sketch, "E14.26.2", {"start": v(-66.1, -18.88) * mm, "mid": v(-64.65, -19.19) * mm, "end": v(-63.16, -19.16) * mm});
            skArc(sketch, "E14.26.3", {"start": v(-66.4, -17.8) * mm, "mid": v(-66.26, -18.34) * mm, "end": v(-66.1, -18.88) * mm});
            skArc(sketch, "E14.26.4", {"start": v(-66.4, -17.8) * mm, "mid": v(-66.55, -17.25) * mm, "end": v(-66.69, -16.7) * mm});
            skArc(sketch, "E14.26.5", {"start": v(-66.69, -16.7) * mm, "mid": v(-65.58, -15.7) * mm, "end": v(-64.28, -14.99) * mm});
            skLineSegment(sketch, "E14.26.6", {"start": v(-64.28, -14.99) * mm, "end": v(-61.2, -14.27) * mm});
            skArc(sketch, "E14.26.7", {"start": v(-61.2, -14.27) * mm, "mid": v(-61.44, -13.27) * mm, "end": v(-61.64, -12.26) * mm});
            skArc(sketch, "E14.27.0", {"start": v(-57.25, -25.94) * mm, "mid": v(-56.82, -26.88) * mm, "end": v(-56.37, -27.8) * mm});
            skLineSegment(sketch, "E14.27.1", {"start": v(-60.12, -27.24) * mm, "end": v(-57.25, -25.94) * mm});
            skArc(sketch, "E14.27.2", {"start": v(-63.08, -27.34) * mm, "mid": v(-61.6, -27.46) * mm, "end": v(-60.12, -27.24) * mm});
            skArc(sketch, "E14.27.3", {"start": v(-63.52, -26.3) * mm, "mid": v(-63.3, -26.83) * mm, "end": v(-63.08, -27.34) * mm});
            skArc(sketch, "E14.27.4", {"start": v(-63.52, -26.3) * mm, "mid": v(-63.73, -25.8) * mm, "end": v(-63.94, -25.27) * mm});
            skArc(sketch, "E14.27.5", {"start": v(-63.94, -25.27) * mm, "mid": v(-62.97, -24.13) * mm, "end": v(-61.77, -23.25) * mm});
            skLineSegment(sketch, "E14.27.6", {"start": v(-61.77, -23.25) * mm, "end": v(-58.82, -22.14) * mm});
            skArc(sketch, "E14.27.7", {"start": v(-58.82, -22.14) * mm, "mid": v(-59.18, -21.18) * mm, "end": v(-59.51, -20.2) * mm});
            skArc(sketch, "E14.28.0", {"start": v(-53.37, -33.19) * mm, "mid": v(-52.83, -34.06) * mm, "end": v(-52.26, -34.92) * mm});
            skLineSegment(sketch, "E14.28.1", {"start": v(-56.05, -34.85) * mm, "end": v(-53.37, -33.19) * mm});
            skArc(sketch, "E14.28.2", {"start": v(-58.97, -35.34) * mm, "mid": v(-57.48, -35.27) * mm, "end": v(-56.05, -34.85) * mm});
            skArc(sketch, "E14.28.3", {"start": v(-59.54, -34.37) * mm, "mid": v(-59.26, -34.86) * mm, "end": v(-58.97, -35.34) * mm});
            skArc(sketch, "E14.28.4", {"start": v(-59.54, -34.37) * mm, "mid": v(-59.82, -33.89) * mm, "end": v(-60.1, -33.4) * mm});
            skArc(sketch, "E14.28.5", {"start": v(-60.1, -33.4) * mm, "mid": v(-59.28, -32.14) * mm, "end": v(-58.2, -31.11) * mm});
            skLineSegment(sketch, "E14.28.6", {"start": v(-58.2, -31.11) * mm, "end": v(-55.43, -29.63) * mm});
            skArc(sketch, "E14.28.7", {"start": v(-55.43, -29.63) * mm, "mid": v(-55.91, -28.72) * mm, "end": v(-56.37, -27.8) * mm});
            skArc(sketch, "E14.29.0", {"start": v(-48.58, -39.87) * mm, "mid": v(-47.93, -40.67) * mm, "end": v(-47.25, -41.44) * mm});
            skLineSegment(sketch, "E14.29.1", {"start": v(-51.02, -41.87) * mm, "end": v(-48.58, -39.87) * mm});
            skArc(sketch, "E14.29.2", {"start": v(-53.85, -42.74) * mm, "mid": v(-52.38, -42.47) * mm, "end": v(-51.02, -41.87) * mm});
            skArc(sketch, "E14.29.3", {"start": v(-54.54, -41.85) * mm, "mid": v(-54.2, -42.3) * mm, "end": v(-53.85, -42.74) * mm});
            skArc(sketch, "E14.29.4", {"start": v(-54.54, -41.85) * mm, "mid": v(-54.89, -41.4) * mm, "end": v(-55.22, -40.95) * mm});
            skArc(sketch, "E14.29.5", {"start": v(-55.22, -40.95) * mm, "mid": v(-54.58, -39.6) * mm, "end": v(-53.65, -38.44) * mm});
            skLineSegment(sketch, "E14.29.6", {"start": v(-53.65, -38.44) * mm, "end": v(-51.09, -36.6) * mm});
            skArc(sketch, "E14.29.7", {"start": v(-51.09, -36.6) * mm, "mid": v(-51.69, -35.77) * mm, "end": v(-52.26, -34.92) * mm});
            skArc(sketch, "E14.30.0", {"start": v(-42.96, -45.87) * mm, "mid": v(-42.21, -46.58) * mm, "end": v(-41.44, -47.25) * mm});
            skLineSegment(sketch, "E14.30.1", {"start": v(-45.12, -48.17) * mm, "end": v(-42.96, -45.87) * mm});
            skArc(sketch, "E14.30.2", {"start": v(-47.81, -49.4) * mm, "mid": v(-46.4, -48.94) * mm, "end": v(-45.12, -48.17) * mm});
            skArc(sketch, "E14.30.3", {"start": v(-48.61, -48.61) * mm, "mid": v(-48.22, -49.01) * mm, "end": v(-47.81, -49.4) * mm});
            skArc(sketch, "E14.30.4", {"start": v(-48.61, -48.61) * mm, "mid": v(-49.01, -48.22) * mm, "end": v(-49.4, -47.81) * mm});
            skArc(sketch, "E14.30.5", {"start": v(-49.4, -47.81) * mm, "mid": v(-48.94, -46.4) * mm, "end": v(-48.17, -45.12) * mm});
            skLineSegment(sketch, "E14.30.6", {"start": v(-48.17, -45.12) * mm, "end": v(-45.87, -42.96) * mm});
            skArc(sketch, "E14.30.7", {"start": v(-45.87, -42.96) * mm, "mid": v(-46.58, -42.21) * mm, "end": v(-47.25, -41.44) * mm});
            skArc(sketch, "E14.31.0", {"start": v(-36.6, -51.09) * mm, "mid": v(-35.77, -51.69) * mm, "end": v(-34.92, -52.26) * mm});
            skLineSegment(sketch, "E14.31.1", {"start": v(-38.44, -53.65) * mm, "end": v(-36.6, -51.09) * mm});
            skArc(sketch, "E14.31.2", {"start": v(-40.95, -55.22) * mm, "mid": v(-39.6, -54.58) * mm, "end": v(-38.44, -53.65) * mm});
            skArc(sketch, "E14.31.3", {"start": v(-41.85, -54.54) * mm, "mid": v(-41.4, -54.89) * mm, "end": v(-40.95, -55.22) * mm});
            skArc(sketch, "E14.31.4", {"start": v(-41.85, -54.54) * mm, "mid": v(-42.3, -54.2) * mm, "end": v(-42.74, -53.85) * mm});
            skArc(sketch, "E14.31.5", {"start": v(-42.74, -53.85) * mm, "mid": v(-42.47, -52.38) * mm, "end": v(-41.87, -51.02) * mm});
            skLineSegment(sketch, "E14.31.6", {"start": v(-41.87, -51.02) * mm, "end": v(-39.87, -48.58) * mm});
            skArc(sketch, "E14.31.7", {"start": v(-39.87, -48.58) * mm, "mid": v(-40.67, -47.93) * mm, "end": v(-41.44, -47.25) * mm});
            skArc(sketch, "E14.32.0", {"start": v(-29.63, -55.43) * mm, "mid": v(-28.72, -55.91) * mm, "end": v(-27.8, -56.37) * mm});
            skLineSegment(sketch, "E14.32.1", {"start": v(-31.11, -58.2) * mm, "end": v(-29.63, -55.43) * mm});
            skArc(sketch, "E14.32.2", {"start": v(-33.4, -60.1) * mm, "mid": v(-32.14, -59.28) * mm, "end": v(-31.11, -58.2) * mm});
            skArc(sketch, "E14.32.3", {"start": v(-34.37, -59.54) * mm, "mid": v(-33.89, -59.82) * mm, "end": v(-33.4, -60.1) * mm});
            skArc(sketch, "E14.32.4", {"start": v(-34.37, -59.54) * mm, "mid": v(-34.86, -59.26) * mm, "end": v(-35.34, -58.97) * mm});
            skArc(sketch, "E14.32.5", {"start": v(-35.34, -58.97) * mm, "mid": v(-35.27, -57.48) * mm, "end": v(-34.85, -56.05) * mm});
            skLineSegment(sketch, "E14.32.6", {"start": v(-34.85, -56.05) * mm, "end": v(-33.19, -53.37) * mm});
            skArc(sketch, "E14.32.7", {"start": v(-33.19, -53.37) * mm, "mid": v(-34.06, -52.83) * mm, "end": v(-34.92, -52.26) * mm});
            skArc(sketch, "E14.33.0", {"start": v(-22.14, -58.82) * mm, "mid": v(-21.18, -59.18) * mm, "end": v(-20.2, -59.51) * mm});
            skLineSegment(sketch, "E14.33.1", {"start": v(-23.25, -61.77) * mm, "end": v(-22.14, -58.82) * mm});
            skArc(sketch, "E14.33.2", {"start": v(-25.27, -63.94) * mm, "mid": v(-24.13, -62.97) * mm, "end": v(-23.25, -61.77) * mm});
            skArc(sketch, "E14.33.3", {"start": v(-26.3, -63.52) * mm, "mid": v(-25.8, -63.73) * mm, "end": v(-25.27, -63.94) * mm});
            skArc(sketch, "E14.33.4", {"start": v(-26.3, -63.52) * mm, "mid": v(-26.83, -63.3) * mm, "end": v(-27.34, -63.08) * mm});
            skArc(sketch, "E14.33.5", {"start": v(-27.34, -63.08) * mm, "mid": v(-27.46, -61.6) * mm, "end": v(-27.24, -60.12) * mm});
            skLineSegment(sketch, "E14.33.6", {"start": v(-27.24, -60.12) * mm, "end": v(-25.94, -57.25) * mm});
            skArc(sketch, "E14.33.7", {"start": v(-25.94, -57.25) * mm, "mid": v(-26.88, -56.82) * mm, "end": v(-27.8, -56.37) * mm});
            skArc(sketch, "E14.34.0", {"start": v(-14.27, -61.2) * mm, "mid": v(-13.27, -61.44) * mm, "end": v(-12.26, -61.64) * mm});
            skLineSegment(sketch, "E14.34.1", {"start": v(-14.99, -64.28) * mm, "end": v(-14.27, -61.2) * mm});
            skArc(sketch, "E14.34.2", {"start": v(-16.7, -66.69) * mm, "mid": v(-15.7, -65.58) * mm, "end": v(-14.99, -64.28) * mm});
            skArc(sketch, "E14.34.3", {"start": v(-17.8, -66.4) * mm, "mid": v(-17.25, -66.55) * mm, "end": v(-16.7, -66.69) * mm});
            skArc(sketch, "E14.34.4", {"start": v(-17.8, -66.4) * mm, "mid": v(-18.34, -66.26) * mm, "end": v(-18.88, -66.1) * mm});
            skArc(sketch, "E14.34.5", {"start": v(-18.88, -66.1) * mm, "mid": v(-19.19, -64.65) * mm, "end": v(-19.16, -63.16) * mm});
            skLineSegment(sketch, "E14.34.6", {"start": v(-19.16, -63.16) * mm, "end": v(-18.24, -60.14) * mm});
            skArc(sketch, "E14.34.7", {"start": v(-18.24, -60.14) * mm, "mid": v(-19.23, -59.85) * mm, "end": v(-20.2, -59.51) * mm});
            skArc(sketch, "E14.35.0", {"start": v(-6.16, -62.55) * mm, "mid": v(-5.14, -62.65) * mm, "end": v(-4.11, -62.72) * mm});
            skLineSegment(sketch, "E14.35.1", {"start": v(-6.47, -65.68) * mm, "end": v(-6.16, -62.55) * mm});
            skArc(sketch, "E14.35.2", {"start": v(-7.86, -68.3) * mm, "mid": v(-7.01, -67.07) * mm, "end": v(-6.47, -65.68) * mm});
            skArc(sketch, "E14.35.3", {"start": v(-8.97, -68.16) * mm, "mid": v(-8.42, -68.24) * mm, "end": v(-7.86, -68.3) * mm});
            skArc(sketch, "E14.35.4", {"start": v(-8.97, -68.16) * mm, "mid": v(-9.53, -68.09) * mm, "end": v(-10.09, -68) * mm});
            skArc(sketch, "E14.35.5", {"start": v(-10.09, -68) * mm, "mid": v(-10.59, -66.6) * mm, "end": v(-10.75, -65.12) * mm});
            skLineSegment(sketch, "E14.35.6", {"start": v(-10.75, -65.12) * mm, "end": v(-10.24, -62.01) * mm});
            skArc(sketch, "E14.35.7", {"start": v(-10.24, -62.01) * mm, "mid": v(-11.25, -61.84) * mm, "end": v(-12.26, -61.64) * mm});
            skArc(sketch, "E14.36.0", {"start": v(2.06, -62.82) * mm, "mid": v(3.08, -62.78) * mm, "end": v(4.11, -62.72) * mm});
            skLineSegment(sketch, "E14.36.1", {"start": v(2.16, -65.96) * mm, "end": v(2.06, -62.82) * mm});
            skArc(sketch, "E14.36.2", {"start": v(1.12, -68.74) * mm, "mid": v(1.8, -67.41) * mm, "end": v(2.16, -65.96) * mm});
            skArc(sketch, "E14.36.3", {"start": v(0, -68.75) * mm, "mid": v(0.56, -68.75) * mm, "end": v(1.12, -68.74) * mm});
            skArc(sketch, "E14.36.4", {"start": v(0, -68.75) * mm, "mid": v(-0.56, -68.75) * mm, "end": v(-1.12, -68.74) * mm});
            skArc(sketch, "E14.36.5", {"start": v(-1.12, -68.74) * mm, "mid": v(-1.8, -67.41) * mm, "end": v(-2.16, -65.96) * mm});
            skLineSegment(sketch, "E14.36.6", {"start": v(-2.16, -65.96) * mm, "end": v(-2.06, -62.82) * mm});
            skArc(sketch, "E14.36.7", {"start": v(-2.06, -62.82) * mm, "mid": v(-3.08, -62.78) * mm, "end": v(-4.11, -62.72) * mm});
            skArc(sketch, "E14.37.0", {"start": v(10.24, -62.01) * mm, "mid": v(11.25, -61.84) * mm, "end": v(12.26, -61.64) * mm});
            skLineSegment(sketch, "E14.37.1", {"start": v(10.75, -65.12) * mm, "end": v(10.24, -62.01) * mm});
            skArc(sketch, "E14.37.2", {"start": v(10.09, -68) * mm, "mid": v(10.59, -66.6) * mm, "end": v(10.75, -65.12) * mm});
            skArc(sketch, "E14.37.3", {"start": v(8.97, -68.16) * mm, "mid": v(9.53, -68.09) * mm, "end": v(10.09, -68) * mm});
            skArc(sketch, "E14.37.4", {"start": v(8.97, -68.16) * mm, "mid": v(8.42, -68.24) * mm, "end": v(7.86, -68.3) * mm});
            skArc(sketch, "E14.37.5", {"start": v(7.86, -68.3) * mm, "mid": v(7.01, -67.07) * mm, "end": v(6.47, -65.68) * mm});
            skLineSegment(sketch, "E14.37.6", {"start": v(6.47, -65.68) * mm, "end": v(6.16, -62.55) * mm});
            skArc(sketch, "E14.37.7", {"start": v(6.16, -62.55) * mm, "mid": v(5.14, -62.65) * mm, "end": v(4.11, -62.72) * mm});
            skArc(sketch, "E14.38.0", {"start": v(18.24, -60.14) * mm, "mid": v(19.23, -59.85) * mm, "end": v(20.2, -59.51) * mm});
            skLineSegment(sketch, "E14.38.1", {"start": v(19.16, -63.16) * mm, "end": v(18.24, -60.14) * mm});
            skArc(sketch, "E14.38.2", {"start": v(18.88, -66.1) * mm, "mid": v(19.19, -64.65) * mm, "end": v(19.16, -63.16) * mm});
            skArc(sketch, "E14.38.3", {"start": v(17.8, -66.4) * mm, "mid": v(18.34, -66.26) * mm, "end": v(18.88, -66.1) * mm});
            skArc(sketch, "E14.38.4", {"start": v(17.8, -66.4) * mm, "mid": v(17.25, -66.55) * mm, "end": v(16.7, -66.69) * mm});
            skArc(sketch, "E14.38.5", {"start": v(16.7, -66.69) * mm, "mid": v(15.7, -65.58) * mm, "end": v(14.99, -64.28) * mm});
            skLineSegment(sketch, "E14.38.6", {"start": v(14.99, -64.28) * mm, "end": v(14.27, -61.2) * mm});
            skArc(sketch, "E14.38.7", {"start": v(14.27, -61.2) * mm, "mid": v(13.27, -61.44) * mm, "end": v(12.26, -61.64) * mm});
            skArc(sketch, "E14.39.0", {"start": v(25.94, -57.25) * mm, "mid": v(26.88, -56.82) * mm, "end": v(27.8, -56.37) * mm});
            skLineSegment(sketch, "E14.39.1", {"start": v(27.24, -60.12) * mm, "end": v(25.94, -57.25) * mm});
            skArc(sketch, "E14.39.2", {"start": v(27.34, -63.08) * mm, "mid": v(27.46, -61.6) * mm, "end": v(27.24, -60.12) * mm});
            skArc(sketch, "E14.39.3", {"start": v(26.3, -63.52) * mm, "mid": v(26.83, -63.3) * mm, "end": v(27.34, -63.08) * mm});
            skArc(sketch, "E14.39.4", {"start": v(26.3, -63.52) * mm, "mid": v(25.8, -63.73) * mm, "end": v(25.27, -63.94) * mm});
            skArc(sketch, "E14.39.5", {"start": v(25.27, -63.94) * mm, "mid": v(24.13, -62.97) * mm, "end": v(23.25, -61.77) * mm});
            skLineSegment(sketch, "E14.39.6", {"start": v(23.25, -61.77) * mm, "end": v(22.14, -58.82) * mm});
            skArc(sketch, "E14.39.7", {"start": v(22.14, -58.82) * mm, "mid": v(21.18, -59.18) * mm, "end": v(20.2, -59.51) * mm});
            skArc(sketch, "E14.40.0", {"start": v(33.19, -53.37) * mm, "mid": v(34.06, -52.83) * mm, "end": v(34.92, -52.26) * mm});
            skLineSegment(sketch, "E14.40.1", {"start": v(34.85, -56.05) * mm, "end": v(33.19, -53.37) * mm});
            skArc(sketch, "E14.40.2", {"start": v(35.34, -58.97) * mm, "mid": v(35.27, -57.48) * mm, "end": v(34.85, -56.05) * mm});
            skArc(sketch, "E14.40.3", {"start": v(34.37, -59.54) * mm, "mid": v(34.86, -59.26) * mm, "end": v(35.34, -58.97) * mm});
            skArc(sketch, "E14.40.4", {"start": v(34.37, -59.54) * mm, "mid": v(33.89, -59.82) * mm, "end": v(33.4, -60.1) * mm});
            skArc(sketch, "E14.40.5", {"start": v(33.4, -60.1) * mm, "mid": v(32.14, -59.28) * mm, "end": v(31.11, -58.2) * mm});
            skLineSegment(sketch, "E14.40.6", {"start": v(31.11, -58.2) * mm, "end": v(29.63, -55.43) * mm});
            skArc(sketch, "E14.40.7", {"start": v(29.63, -55.43) * mm, "mid": v(28.72, -55.91) * mm, "end": v(27.8, -56.37) * mm});
            skArc(sketch, "E14.41.0", {"start": v(39.87, -48.58) * mm, "mid": v(40.67, -47.93) * mm, "end": v(41.44, -47.25) * mm});
            skLineSegment(sketch, "E14.41.1", {"start": v(41.87, -51.02) * mm, "end": v(39.87, -48.58) * mm});
            skArc(sketch, "E14.41.2", {"start": v(42.74, -53.85) * mm, "mid": v(42.47, -52.38) * mm, "end": v(41.87, -51.02) * mm});
            skArc(sketch, "E14.41.3", {"start": v(41.85, -54.54) * mm, "mid": v(42.3, -54.2) * mm, "end": v(42.74, -53.85) * mm});
            skArc(sketch, "E14.41.4", {"start": v(41.85, -54.54) * mm, "mid": v(41.4, -54.89) * mm, "end": v(40.95, -55.22) * mm});
            skArc(sketch, "E14.41.5", {"start": v(40.95, -55.22) * mm, "mid": v(39.6, -54.58) * mm, "end": v(38.44, -53.65) * mm});
            skLineSegment(sketch, "E14.41.6", {"start": v(38.44, -53.65) * mm, "end": v(36.6, -51.09) * mm});
            skArc(sketch, "E14.41.7", {"start": v(36.6, -51.09) * mm, "mid": v(35.77, -51.69) * mm, "end": v(34.92, -52.26) * mm});
            skArc(sketch, "E14.42.0", {"start": v(45.87, -42.96) * mm, "mid": v(46.58, -42.21) * mm, "end": v(47.25, -41.44) * mm});
            skLineSegment(sketch, "E14.42.1", {"start": v(48.17, -45.12) * mm, "end": v(45.87, -42.96) * mm});
            skArc(sketch, "E14.42.2", {"start": v(49.4, -47.81) * mm, "mid": v(48.94, -46.4) * mm, "end": v(48.17, -45.12) * mm});
            skArc(sketch, "E14.42.3", {"start": v(48.61, -48.61) * mm, "mid": v(49.01, -48.22) * mm, "end": v(49.4, -47.81) * mm});
            skArc(sketch, "E14.42.4", {"start": v(48.61, -48.61) * mm, "mid": v(48.22, -49.01) * mm, "end": v(47.81, -49.4) * mm});
            skArc(sketch, "E14.42.5", {"start": v(47.81, -49.4) * mm, "mid": v(46.4, -48.94) * mm, "end": v(45.12, -48.17) * mm});
            skLineSegment(sketch, "E14.42.6", {"start": v(45.12, -48.17) * mm, "end": v(42.96, -45.87) * mm});
            skArc(sketch, "E14.42.7", {"start": v(42.96, -45.87) * mm, "mid": v(42.21, -46.58) * mm, "end": v(41.44, -47.25) * mm});
            skArc(sketch, "E14.43.0", {"start": v(51.09, -36.6) * mm, "mid": v(51.69, -35.77) * mm, "end": v(52.26, -34.92) * mm});
            skLineSegment(sketch, "E14.43.1", {"start": v(53.65, -38.44) * mm, "end": v(51.09, -36.6) * mm});
            skArc(sketch, "E14.43.2", {"start": v(55.22, -40.95) * mm, "mid": v(54.58, -39.6) * mm, "end": v(53.65, -38.44) * mm});
            skArc(sketch, "E14.43.3", {"start": v(54.54, -41.85) * mm, "mid": v(54.89, -41.4) * mm, "end": v(55.22, -40.95) * mm});
            skArc(sketch, "E14.43.4", {"start": v(54.54, -41.85) * mm, "mid": v(54.2, -42.3) * mm, "end": v(53.85, -42.74) * mm});
            skArc(sketch, "E14.43.5", {"start": v(53.85, -42.74) * mm, "mid": v(52.38, -42.47) * mm, "end": v(51.02, -41.87) * mm});
            skLineSegment(sketch, "E14.43.6", {"start": v(51.02, -41.87) * mm, "end": v(48.58, -39.87) * mm});
            skArc(sketch, "E14.43.7", {"start": v(48.58, -39.87) * mm, "mid": v(47.93, -40.67) * mm, "end": v(47.25, -41.44) * mm});
            skArc(sketch, "E14.44.0", {"start": v(55.43, -29.63) * mm, "mid": v(55.91, -28.72) * mm, "end": v(56.37, -27.8) * mm});
            skLineSegment(sketch, "E14.44.1", {"start": v(58.2, -31.11) * mm, "end": v(55.43, -29.63) * mm});
            skArc(sketch, "E14.44.2", {"start": v(60.1, -33.4) * mm, "mid": v(59.28, -32.14) * mm, "end": v(58.2, -31.11) * mm});
            skArc(sketch, "E14.44.3", {"start": v(59.54, -34.37) * mm, "mid": v(59.82, -33.89) * mm, "end": v(60.1, -33.4) * mm});
            skArc(sketch, "E14.44.4", {"start": v(59.54, -34.37) * mm, "mid": v(59.26, -34.86) * mm, "end": v(58.97, -35.34) * mm});
            skArc(sketch, "E14.44.5", {"start": v(58.97, -35.34) * mm, "mid": v(57.48, -35.27) * mm, "end": v(56.05, -34.85) * mm});
            skLineSegment(sketch, "E14.44.6", {"start": v(56.05, -34.85) * mm, "end": v(53.37, -33.19) * mm});
            skArc(sketch, "E14.44.7", {"start": v(53.37, -33.19) * mm, "mid": v(52.83, -34.06) * mm, "end": v(52.26, -34.92) * mm});
            skArc(sketch, "E14.45.0", {"start": v(58.82, -22.14) * mm, "mid": v(59.18, -21.18) * mm, "end": v(59.51, -20.2) * mm});
            skLineSegment(sketch, "E14.45.1", {"start": v(61.77, -23.25) * mm, "end": v(58.82, -22.14) * mm});
            skArc(sketch, "E14.45.2", {"start": v(63.94, -25.27) * mm, "mid": v(62.97, -24.13) * mm, "end": v(61.77, -23.25) * mm});
            skArc(sketch, "E14.45.3", {"start": v(63.52, -26.3) * mm, "mid": v(63.73, -25.8) * mm, "end": v(63.94, -25.27) * mm});
            skArc(sketch, "E14.45.4", {"start": v(63.52, -26.3) * mm, "mid": v(63.3, -26.83) * mm, "end": v(63.08, -27.34) * mm});
            skArc(sketch, "E14.45.5", {"start": v(63.08, -27.34) * mm, "mid": v(61.6, -27.46) * mm, "end": v(60.12, -27.24) * mm});
            skLineSegment(sketch, "E14.45.6", {"start": v(60.12, -27.24) * mm, "end": v(57.25, -25.94) * mm});
            skArc(sketch, "E14.45.7", {"start": v(57.25, -25.94) * mm, "mid": v(56.82, -26.88) * mm, "end": v(56.37, -27.8) * mm});
            skArc(sketch, "E14.46.0", {"start": v(61.2, -14.27) * mm, "mid": v(61.44, -13.27) * mm, "end": v(61.64, -12.26) * mm});
            skLineSegment(sketch, "E14.46.1", {"start": v(64.28, -14.99) * mm, "end": v(61.2, -14.27) * mm});
            skArc(sketch, "E14.46.2", {"start": v(66.69, -16.7) * mm, "mid": v(65.58, -15.7) * mm, "end": v(64.28, -14.99) * mm});
            skArc(sketch, "E14.46.3", {"start": v(66.4, -17.8) * mm, "mid": v(66.55, -17.25) * mm, "end": v(66.69, -16.7) * mm});
            skArc(sketch, "E14.46.4", {"start": v(66.4, -17.8) * mm, "mid": v(66.26, -18.34) * mm, "end": v(66.1, -18.88) * mm});
            skArc(sketch, "E14.46.5", {"start": v(66.1, -18.88) * mm, "mid": v(64.65, -19.19) * mm, "end": v(63.16, -19.16) * mm});
            skLineSegment(sketch, "E14.46.6", {"start": v(63.16, -19.16) * mm, "end": v(60.14, -18.24) * mm});
            skArc(sketch, "E14.46.7", {"start": v(60.14, -18.24) * mm, "mid": v(59.85, -19.23) * mm, "end": v(59.51, -20.2) * mm});
            skArc(sketch, "E14.47.0", {"start": v(62.55, -6.16) * mm, "mid": v(62.65, -5.14) * mm, "end": v(62.72, -4.11) * mm});
            skLineSegment(sketch, "E14.47.1", {"start": v(65.68, -6.47) * mm, "end": v(62.55, -6.16) * mm});
            skArc(sketch, "E14.47.2", {"start": v(68.3, -7.86) * mm, "mid": v(67.07, -7.01) * mm, "end": v(65.68, -6.47) * mm});
            skArc(sketch, "E14.47.3", {"start": v(68.16, -8.97) * mm, "mid": v(68.24, -8.42) * mm, "end": v(68.3, -7.86) * mm});
            skArc(sketch, "E14.47.4", {"start": v(68.16, -8.97) * mm, "mid": v(68.09, -9.53) * mm, "end": v(68, -10.09) * mm});
            skArc(sketch, "E14.47.5", {"start": v(68, -10.09) * mm, "mid": v(66.6, -10.59) * mm, "end": v(65.12, -10.75) * mm});
            skLineSegment(sketch, "E14.47.6", {"start": v(65.12, -10.75) * mm, "end": v(62.01, -10.24) * mm});
            skArc(sketch, "E14.47.7", {"start": v(62.01, -10.24) * mm, "mid": v(61.84, -11.25) * mm, "end": v(61.64, -12.26) * mm});
            skSolve(sketch);
        }
        {
            var Q0;
            Q0 = qSketchRegion(id + "F0", true);
            var Q1;
            Q1=makeQuery(id+"F0.imprint","IMPRINT",FACE,{"disambiguationData":[TD([[makeQuery(id+"F0.imprint","IMPRINT",EDGE,{"derivedFrom":sQuery(id+"F0.wireOp",EDGE,"SGI266rr-FQQk-z7iK-ldje-f7bPt8xBOslD")}),-1.0]])]});
            extrude(context, id + "F1", {"entities" : qUnion([Q0, Q1]), "endBound" : BoundingType.SYMMETRIC, "depth" : 15 * mm});
        }
        {
            var Q0;
            Q0=makeQuery(id+"F1.opExtrude","CAP_FACE",FACE,{"disambiguationData":[OSD([sQuery(id+"F0.wireOp",EDGE,"E0"),sQuery(id+"F0.wireOp",EDGE,"E4"),sQuery(id+"F0.wireOp",EDGE,"E5"),sQuery(id+"F0.wireOp",EDGE,"E6"),sQuery(id+"F0.wireOp",EDGE,"E7"),sQuery(id+"F0.wireOp",EDGE,"E9.MirrorCS"),sQuery(id+"F0.wireOp",EDGE,"E10.MirrorCS"),sQuery(id+"F0.wireOp",EDGE,"E11.MirrorCS"),sQuery(id+"F0.wireOp",EDGE,"E12.MirrorCS"),sQuery(id+"F0.wireOp",EDGE,"E14.1.0"),sQuery(id+"F0.wireOp",EDGE,"E14.1.1"),sQuery(id+"F0.wireOp",EDGE,"E14.1.2"),sQuery(id+"F0.wireOp",EDGE,"E14.1.3"),sQuery(id+"F0.wireOp",EDGE,"E14.1.4"),sQuery(id+"F0.wireOp",EDGE,"E14.1.5"),sQuery(id+"F0.wireOp",EDGE,"E14.1.6"),sQuery(id+"F0.wireOp",EDGE,"E14.1.7"),sQuery(id+"F0.wireOp",EDGE,"E14.2.0"),sQuery(id+"F0.wireOp",EDGE,"E14.2.1"),sQuery(id+"F0.wireOp",EDGE,"E14.2.2"),sQuery(id+"F0.wireOp",EDGE,"E14.2.3"),sQuery(id+"F0.wireOp",EDGE,"E14.2.4"),sQuery(id+"F0.wireOp",EDGE,"E14.2.5"),sQuery(id+"F0.wireOp",EDGE,"E14.2.6"),sQuery(id+"F0.wireOp",EDGE,"E14.2.7"),sQuery(id+"F0.wireOp",EDGE,"E14.3.0"),sQuery(id+"F0.wireOp",EDGE,"E14.3.1"),sQuery(id+"F0.wireOp",EDGE,"E14.3.2"),sQuery(id+"F0.wireOp",EDGE,"E14.3.3"),sQuery(id+"F0.wireOp",EDGE,"E14.3.4"),sQuery(id+"F0.wireOp",EDGE,"E14.3.5"),sQuery(id+"F0.wireOp",EDGE,"E14.3.6"),sQuery(id+"F0.wireOp",EDGE,"E14.3.7"),sQuery(id+"F0.wireOp",EDGE,"E14.4.0"),sQuery(id+"F0.wireOp",EDGE,"E14.4.1"),sQuery(id+"F0.wireOp",EDGE,"E14.4.2"),sQuery(id+"F0.wireOp",EDGE,"E14.4.3"),sQuery(id+"F0.wireOp",EDGE,"E14.4.4"),sQuery(id+"F0.wireOp",EDGE,"E14.4.5"),sQuery(id+"F0.wireOp",EDGE,"E14.4.6"),sQuery(id+"F0.wireOp",EDGE,"E14.4.7"),sQuery(id+"F0.wireOp",EDGE,"E14.5.0"),sQuery(id+"F0.wireOp",EDGE,"E14.5.1"),sQuery(id+"F0.wireOp",EDGE,"E14.5.2"),sQuery(id+"F0.wireOp",EDGE,"E14.5.3"),sQuery(id+"F0.wireOp",EDGE,"E14.5.4"),sQuery(id+"F0.wireOp",EDGE,"E14.5.5"),sQuery(id+"F0.wireOp",EDGE,"E14.5.6"),sQuery(id+"F0.wireOp",EDGE,"E14.5.7"),sQuery(id+"F0.wireOp",EDGE,"E14.6.0"),sQuery(id+"F0.wireOp",EDGE,"E14.6.1"),sQuery(id+"F0.wireOp",EDGE,"E14.6.2"),sQuery(id+"F0.wireOp",EDGE,"E14.6.3"),sQuery(id+"F0.wireOp",EDGE,"E14.6.4"),sQuery(id+"F0.wireOp",EDGE,"E14.6.5"),sQuery(id+"F0.wireOp",EDGE,"E14.6.6"),sQuery(id+"F0.wireOp",EDGE,"E14.6.7"),sQuery(id+"F0.wireOp",EDGE,"E14.7.0"),sQuery(id+"F0.wireOp",EDGE,"E14.7.1"),sQuery(id+"F0.wireOp",EDGE,"E14.7.2"),sQuery(id+"F0.wireOp",EDGE,"E14.7.3"),sQuery(id+"F0.wireOp",EDGE,"E14.7.4"),sQuery(id+"F0.wireOp",EDGE,"E14.7.5"),sQuery(id+"F0.wireOp",EDGE,"E14.7.6"),sQuery(id+"F0.wireOp",EDGE,"E14.7.7"),sQuery(id+"F0.wireOp",EDGE,"E14.8.0"),sQuery(id+"F0.wireOp",EDGE,"E14.8.1"),sQuery(id+"F0.wireOp",EDGE,"E14.8.2"),sQuery(id+"F0.wireOp",EDGE,"E14.8.3"),sQuery(id+"F0.wireOp",EDGE,"E14.8.4"),sQuery(id+"F0.wireOp",EDGE,"E14.8.5"),sQuery(id+"F0.wireOp",EDGE,"E14.8.6"),sQuery(id+"F0.wireOp",EDGE,"E14.8.7"),sQuery(id+"F0.wireOp",EDGE,"E14.9.0"),sQuery(id+"F0.wireOp",EDGE,"E14.9.1"),sQuery(id+"F0.wireOp",EDGE,"E14.9.2"),sQuery(id+"F0.wireOp",EDGE,"E14.9.3"),sQuery(id+"F0.wireOp",EDGE,"E14.9.4"),sQuery(id+"F0.wireOp",EDGE,"E14.9.5"),sQuery(id+"F0.wireOp",EDGE,"E14.9.6"),sQuery(id+"F0.wireOp",EDGE,"E14.9.7"),sQuery(id+"F0.wireOp",EDGE,"E14.10.0"),sQuery(id+"F0.wireOp",EDGE,"E14.10.1"),sQuery(id+"F0.wireOp",EDGE,"E14.10.2"),sQuery(id+"F0.wireOp",EDGE,"E14.10.3"),sQuery(id+"F0.wireOp",EDGE,"E14.10.4"),sQuery(id+"F0.wireOp",EDGE,"E14.10.5"),sQuery(id+"F0.wireOp",EDGE,"E14.10.6"),sQuery(id+"F0.wireOp",EDGE,"E14.10.7"),sQuery(id+"F0.wireOp",EDGE,"E14.11.0"),sQuery(id+"F0.wireOp",EDGE,"E14.11.1"),sQuery(id+"F0.wireOp",EDGE,"E14.11.2"),sQuery(id+"F0.wireOp",EDGE,"E14.11.3"),sQuery(id+"F0.wireOp",EDGE,"E14.11.4"),sQuery(id+"F0.wireOp",EDGE,"E14.11.5"),sQuery(id+"F0.wireOp",EDGE,"E14.11.6"),sQuery(id+"F0.wireOp",EDGE,"E14.11.7"),sQuery(id+"F0.wireOp",EDGE,"E14.12.0"),sQuery(id+"F0.wireOp",EDGE,"E14.12.1"),sQuery(id+"F0.wireOp",EDGE,"E14.12.2"),sQuery(id+"F0.wireOp",EDGE,"E14.12.3"),sQuery(id+"F0.wireOp",EDGE,"E14.12.4"),sQuery(id+"F0.wireOp",EDGE,"E14.12.5"),sQuery(id+"F0.wireOp",EDGE,"E14.12.6"),sQuery(id+"F0.wireOp",EDGE,"E14.12.7"),sQuery(id+"F0.wireOp",EDGE,"E14.13.0"),sQuery(id+"F0.wireOp",EDGE,"E14.13.1"),sQuery(id+"F0.wireOp",EDGE,"E14.13.2"),sQuery(id+"F0.wireOp",EDGE,"E14.13.3"),sQuery(id+"F0.wireOp",EDGE,"E14.13.4"),sQuery(id+"F0.wireOp",EDGE,"E14.13.5"),sQuery(id+"F0.wireOp",EDGE,"E14.13.6"),sQuery(id+"F0.wireOp",EDGE,"E14.13.7"),sQuery(id+"F0.wireOp",EDGE,"E14.14.0"),sQuery(id+"F0.wireOp",EDGE,"E14.14.1"),sQuery(id+"F0.wireOp",EDGE,"E14.14.2"),sQuery(id+"F0.wireOp",EDGE,"E14.14.3"),sQuery(id+"F0.wireOp",EDGE,"E14.14.4"),sQuery(id+"F0.wireOp",EDGE,"E14.14.5"),sQuery(id+"F0.wireOp",EDGE,"E14.14.6"),sQuery(id+"F0.wireOp",EDGE,"E14.14.7"),sQuery(id+"F0.wireOp",EDGE,"E14.15.0"),sQuery(id+"F0.wireOp",EDGE,"E14.15.1"),sQuery(id+"F0.wireOp",EDGE,"E14.15.2"),sQuery(id+"F0.wireOp",EDGE,"E14.15.3"),sQuery(id+"F0.wireOp",EDGE,"E14.15.4"),sQuery(id+"F0.wireOp",EDGE,"E14.15.5"),sQuery(id+"F0.wireOp",EDGE,"E14.15.6"),sQuery(id+"F0.wireOp",EDGE,"E14.15.7"),sQuery(id+"F0.wireOp",EDGE,"E14.16.0"),sQuery(id+"F0.wireOp",EDGE,"E14.16.1"),sQuery(id+"F0.wireOp",EDGE,"E14.16.2"),sQuery(id+"F0.wireOp",EDGE,"E14.16.3"),sQuery(id+"F0.wireOp",EDGE,"E14.16.4"),sQuery(id+"F0.wireOp",EDGE,"E14.16.5"),sQuery(id+"F0.wireOp",EDGE,"E14.16.6"),sQuery(id+"F0.wireOp",EDGE,"E14.16.7"),sQuery(id+"F0.wireOp",EDGE,"E14.17.0"),sQuery(id+"F0.wireOp",EDGE,"E14.17.1"),sQuery(id+"F0.wireOp",EDGE,"E14.17.2"),sQuery(id+"F0.wireOp",EDGE,"E14.17.3"),sQuery(id+"F0.wireOp",EDGE,"E14.17.4"),sQuery(id+"F0.wireOp",EDGE,"E14.17.5"),sQuery(id+"F0.wireOp",EDGE,"E14.17.6"),sQuery(id+"F0.wireOp",EDGE,"E14.17.7"),sQuery(id+"F0.wireOp",EDGE,"E14.18.0"),sQuery(id+"F0.wireOp",EDGE,"E14.18.1"),sQuery(id+"F0.wireOp",EDGE,"E14.18.2"),sQuery(id+"F0.wireOp",EDGE,"E14.18.3"),sQuery(id+"F0.wireOp",EDGE,"E14.18.4"),sQuery(id+"F0.wireOp",EDGE,"E14.18.5"),sQuery(id+"F0.wireOp",EDGE,"E14.18.6"),sQuery(id+"F0.wireOp",EDGE,"E14.18.7"),sQuery(id+"F0.wireOp",EDGE,"E14.19.0"),sQuery(id+"F0.wireOp",EDGE,"E14.19.1"),sQuery(id+"F0.wireOp",EDGE,"E14.19.2"),sQuery(id+"F0.wireOp",EDGE,"E14.19.3"),sQuery(id+"F0.wireOp",EDGE,"E14.19.4"),sQuery(id+"F0.wireOp",EDGE,"E14.19.5"),sQuery(id+"F0.wireOp",EDGE,"E14.19.6"),sQuery(id+"F0.wireOp",EDGE,"E14.19.7"),sQuery(id+"F0.wireOp",EDGE,"E14.20.0"),sQuery(id+"F0.wireOp",EDGE,"E14.20.1"),sQuery(id+"F0.wireOp",EDGE,"E14.20.2"),sQuery(id+"F0.wireOp",EDGE,"E14.20.3"),sQuery(id+"F0.wireOp",EDGE,"E14.20.4"),sQuery(id+"F0.wireOp",EDGE,"E14.20.5"),sQuery(id+"F0.wireOp",EDGE,"E14.20.6"),sQuery(id+"F0.wireOp",EDGE,"E14.20.7"),sQuery(id+"F0.wireOp",EDGE,"E14.21.0"),sQuery(id+"F0.wireOp",EDGE,"E14.21.1"),sQuery(id+"F0.wireOp",EDGE,"E14.21.2"),sQuery(id+"F0.wireOp",EDGE,"E14.21.3"),sQuery(id+"F0.wireOp",EDGE,"E14.21.4"),sQuery(id+"F0.wireOp",EDGE,"E14.21.5"),sQuery(id+"F0.wireOp",EDGE,"E14.21.6"),sQuery(id+"F0.wireOp",EDGE,"E14.21.7"),sQuery(id+"F0.wireOp",EDGE,"E14.22.0"),sQuery(id+"F0.wireOp",EDGE,"E14.22.1"),sQuery(id+"F0.wireOp",EDGE,"E14.22.2"),sQuery(id+"F0.wireOp",EDGE,"E14.22.3"),sQuery(id+"F0.wireOp",EDGE,"E14.22.4"),sQuery(id+"F0.wireOp",EDGE,"E14.22.5"),sQuery(id+"F0.wireOp",EDGE,"E14.22.6"),sQuery(id+"F0.wireOp",EDGE,"E14.22.7"),sQuery(id+"F0.wireOp",EDGE,"E14.23.0"),sQuery(id+"F0.wireOp",EDGE,"E14.23.1"),sQuery(id+"F0.wireOp",EDGE,"E14.23.2"),sQuery(id+"F0.wireOp",EDGE,"E14.23.3"),sQuery(id+"F0.wireOp",EDGE,"E14.23.4"),sQuery(id+"F0.wireOp",EDGE,"E14.23.5"),sQuery(id+"F0.wireOp",EDGE,"E14.23.6"),sQuery(id+"F0.wireOp",EDGE,"E14.23.7"),sQuery(id+"F0.wireOp",EDGE,"E14.24.0"),sQuery(id+"F0.wireOp",EDGE,"E14.24.1"),sQuery(id+"F0.wireOp",EDGE,"E14.24.2"),sQuery(id+"F0.wireOp",EDGE,"E14.24.3"),sQuery(id+"F0.wireOp",EDGE,"E14.24.4"),sQuery(id+"F0.wireOp",EDGE,"E14.24.5"),sQuery(id+"F0.wireOp",EDGE,"E14.24.6"),sQuery(id+"F0.wireOp",EDGE,"E14.24.7"),sQuery(id+"F0.wireOp",EDGE,"E14.25.0"),sQuery(id+"F0.wireOp",EDGE,"E14.25.1"),sQuery(id+"F0.wireOp",EDGE,"E14.25.2"),sQuery(id+"F0.wireOp",EDGE,"E14.25.3"),sQuery(id+"F0.wireOp",EDGE,"E14.25.4"),sQuery(id+"F0.wireOp",EDGE,"E14.25.5"),sQuery(id+"F0.wireOp",EDGE,"E14.25.6"),sQuery(id+"F0.wireOp",EDGE,"E14.25.7"),sQuery(id+"F0.wireOp",EDGE,"E14.26.0"),sQuery(id+"F0.wireOp",EDGE,"E14.26.1"),sQuery(id+"F0.wireOp",EDGE,"E14.26.2"),sQuery(id+"F0.wireOp",EDGE,"E14.26.3"),sQuery(id+"F0.wireOp",EDGE,"E14.26.4"),sQuery(id+"F0.wireOp",EDGE,"E14.26.5"),sQuery(id+"F0.wireOp",EDGE,"E14.26.6"),sQuery(id+"F0.wireOp",EDGE,"E14.26.7"),sQuery(id+"F0.wireOp",EDGE,"E14.27.0"),sQuery(id+"F0.wireOp",EDGE,"E14.27.1"),sQuery(id+"F0.wireOp",EDGE,"E14.27.2"),sQuery(id+"F0.wireOp",EDGE,"E14.27.3"),sQuery(id+"F0.wireOp",EDGE,"E14.27.4"),sQuery(id+"F0.wireOp",EDGE,"E14.27.5"),sQuery(id+"F0.wireOp",EDGE,"E14.27.6"),sQuery(id+"F0.wireOp",EDGE,"E14.27.7"),sQuery(id+"F0.wireOp",EDGE,"E14.28.0"),sQuery(id+"F0.wireOp",EDGE,"E14.28.1"),sQuery(id+"F0.wireOp",EDGE,"E14.28.2"),sQuery(id+"F0.wireOp",EDGE,"E14.28.3"),sQuery(id+"F0.wireOp",EDGE,"E14.28.4"),sQuery(id+"F0.wireOp",EDGE,"E14.28.5"),sQuery(id+"F0.wireOp",EDGE,"E14.28.6"),sQuery(id+"F0.wireOp",EDGE,"E14.28.7"),sQuery(id+"F0.wireOp",EDGE,"E14.29.0"),sQuery(id+"F0.wireOp",EDGE,"E14.29.1"),sQuery(id+"F0.wireOp",EDGE,"E14.29.2"),sQuery(id+"F0.wireOp",EDGE,"E14.29.3"),sQuery(id+"F0.wireOp",EDGE,"E14.29.4"),sQuery(id+"F0.wireOp",EDGE,"E14.29.5"),sQuery(id+"F0.wireOp",EDGE,"E14.29.6"),sQuery(id+"F0.wireOp",EDGE,"E14.29.7"),sQuery(id+"F0.wireOp",EDGE,"E14.30.0"),sQuery(id+"F0.wireOp",EDGE,"E14.30.1"),sQuery(id+"F0.wireOp",EDGE,"E14.30.2"),sQuery(id+"F0.wireOp",EDGE,"E14.30.3"),sQuery(id+"F0.wireOp",EDGE,"E14.30.4"),sQuery(id+"F0.wireOp",EDGE,"E14.30.5"),sQuery(id+"F0.wireOp",EDGE,"E14.30.6"),sQuery(id+"F0.wireOp",EDGE,"E14.30.7"),sQuery(id+"F0.wireOp",EDGE,"E14.31.0"),sQuery(id+"F0.wireOp",EDGE,"E14.31.1"),sQuery(id+"F0.wireOp",EDGE,"E14.31.2"),sQuery(id+"F0.wireOp",EDGE,"E14.31.3"),sQuery(id+"F0.wireOp",EDGE,"E14.31.4"),sQuery(id+"F0.wireOp",EDGE,"E14.31.5"),sQuery(id+"F0.wireOp",EDGE,"E14.31.6"),sQuery(id+"F0.wireOp",EDGE,"E14.31.7"),sQuery(id+"F0.wireOp",EDGE,"E14.32.0"),sQuery(id+"F0.wireOp",EDGE,"E14.32.1"),sQuery(id+"F0.wireOp",EDGE,"E14.32.2"),sQuery(id+"F0.wireOp",EDGE,"E14.32.3"),sQuery(id+"F0.wireOp",EDGE,"E14.32.4"),sQuery(id+"F0.wireOp",EDGE,"E14.32.5"),sQuery(id+"F0.wireOp",EDGE,"E14.32.6"),sQuery(id+"F0.wireOp",EDGE,"E14.32.7"),sQuery(id+"F0.wireOp",EDGE,"E14.33.0"),sQuery(id+"F0.wireOp",EDGE,"E14.33.1"),sQuery(id+"F0.wireOp",EDGE,"E14.33.2"),sQuery(id+"F0.wireOp",EDGE,"E14.33.3"),sQuery(id+"F0.wireOp",EDGE,"E14.33.4"),sQuery(id+"F0.wireOp",EDGE,"E14.33.5"),sQuery(id+"F0.wireOp",EDGE,"E14.33.6"),sQuery(id+"F0.wireOp",EDGE,"E14.33.7"),sQuery(id+"F0.wireOp",EDGE,"E14.34.0"),sQuery(id+"F0.wireOp",EDGE,"E14.34.1"),sQuery(id+"F0.wireOp",EDGE,"E14.34.2"),sQuery(id+"F0.wireOp",EDGE,"E14.34.3"),sQuery(id+"F0.wireOp",EDGE,"E14.34.4"),sQuery(id+"F0.wireOp",EDGE,"E14.34.5"),sQuery(id+"F0.wireOp",EDGE,"E14.34.6"),sQuery(id+"F0.wireOp",EDGE,"E14.34.7"),sQuery(id+"F0.wireOp",EDGE,"E14.35.0"),sQuery(id+"F0.wireOp",EDGE,"E14.35.1"),sQuery(id+"F0.wireOp",EDGE,"E14.35.2"),sQuery(id+"F0.wireOp",EDGE,"E14.35.3"),sQuery(id+"F0.wireOp",EDGE,"E14.35.4"),sQuery(id+"F0.wireOp",EDGE,"E14.35.5"),sQuery(id+"F0.wireOp",EDGE,"E14.35.6"),sQuery(id+"F0.wireOp",EDGE,"E14.35.7"),sQuery(id+"F0.wireOp",EDGE,"E14.36.0"),sQuery(id+"F0.wireOp",EDGE,"E14.36.1"),sQuery(id+"F0.wireOp",EDGE,"E14.36.2"),sQuery(id+"F0.wireOp",EDGE,"E14.36.3"),sQuery(id+"F0.wireOp",EDGE,"E14.36.4"),sQuery(id+"F0.wireOp",EDGE,"E14.36.5"),sQuery(id+"F0.wireOp",EDGE,"E14.36.6"),sQuery(id+"F0.wireOp",EDGE,"E14.36.7"),sQuery(id+"F0.wireOp",EDGE,"E14.37.0"),sQuery(id+"F0.wireOp",EDGE,"E14.37.1"),sQuery(id+"F0.wireOp",EDGE,"E14.37.2"),sQuery(id+"F0.wireOp",EDGE,"E14.37.3"),sQuery(id+"F0.wireOp",EDGE,"E14.37.4"),sQuery(id+"F0.wireOp",EDGE,"E14.37.5"),sQuery(id+"F0.wireOp",EDGE,"E14.37.6"),sQuery(id+"F0.wireOp",EDGE,"E14.37.7"),sQuery(id+"F0.wireOp",EDGE,"E14.38.0"),sQuery(id+"F0.wireOp",EDGE,"E14.38.1"),sQuery(id+"F0.wireOp",EDGE,"E14.38.2"),sQuery(id+"F0.wireOp",EDGE,"E14.38.3"),sQuery(id+"F0.wireOp",EDGE,"E14.38.4"),sQuery(id+"F0.wireOp",EDGE,"E14.38.5"),sQuery(id+"F0.wireOp",EDGE,"E14.38.6"),sQuery(id+"F0.wireOp",EDGE,"E14.38.7"),sQuery(id+"F0.wireOp",EDGE,"E14.39.0"),sQuery(id+"F0.wireOp",EDGE,"E14.39.1"),sQuery(id+"F0.wireOp",EDGE,"E14.39.2"),sQuery(id+"F0.wireOp",EDGE,"E14.39.3"),sQuery(id+"F0.wireOp",EDGE,"E14.39.4"),sQuery(id+"F0.wireOp",EDGE,"E14.39.5"),sQuery(id+"F0.wireOp",EDGE,"E14.39.6"),sQuery(id+"F0.wireOp",EDGE,"E14.39.7"),sQuery(id+"F0.wireOp",EDGE,"E14.40.0"),sQuery(id+"F0.wireOp",EDGE,"E14.40.1"),sQuery(id+"F0.wireOp",EDGE,"E14.40.2"),sQuery(id+"F0.wireOp",EDGE,"E14.40.3"),sQuery(id+"F0.wireOp",EDGE,"E14.40.4"),sQuery(id+"F0.wireOp",EDGE,"E14.40.5"),sQuery(id+"F0.wireOp",EDGE,"E14.40.6"),sQuery(id+"F0.wireOp",EDGE,"E14.40.7"),sQuery(id+"F0.wireOp",EDGE,"E14.41.0"),sQuery(id+"F0.wireOp",EDGE,"E14.41.1"),sQuery(id+"F0.wireOp",EDGE,"E14.41.2"),sQuery(id+"F0.wireOp",EDGE,"E14.41.3"),sQuery(id+"F0.wireOp",EDGE,"E14.41.4"),sQuery(id+"F0.wireOp",EDGE,"E14.41.5"),sQuery(id+"F0.wireOp",EDGE,"E14.41.6"),sQuery(id+"F0.wireOp",EDGE,"E14.41.7"),sQuery(id+"F0.wireOp",EDGE,"E14.42.0"),sQuery(id+"F0.wireOp",EDGE,"E14.42.1"),sQuery(id+"F0.wireOp",EDGE,"E14.42.2"),sQuery(id+"F0.wireOp",EDGE,"E14.42.3"),sQuery(id+"F0.wireOp",EDGE,"E14.42.4"),sQuery(id+"F0.wireOp",EDGE,"E14.42.5"),sQuery(id+"F0.wireOp",EDGE,"E14.42.6"),sQuery(id+"F0.wireOp",EDGE,"E14.42.7"),sQuery(id+"F0.wireOp",EDGE,"E14.43.0"),sQuery(id+"F0.wireOp",EDGE,"E14.43.1"),sQuery(id+"F0.wireOp",EDGE,"E14.43.2"),sQuery(id+"F0.wireOp",EDGE,"E14.43.3"),sQuery(id+"F0.wireOp",EDGE,"E14.43.4"),sQuery(id+"F0.wireOp",EDGE,"E14.43.5"),sQuery(id+"F0.wireOp",EDGE,"E14.43.6"),sQuery(id+"F0.wireOp",EDGE,"E14.43.7"),sQuery(id+"F0.wireOp",EDGE,"E14.44.0"),sQuery(id+"F0.wireOp",EDGE,"E14.44.1"),sQuery(id+"F0.wireOp",EDGE,"E14.44.2"),sQuery(id+"F0.wireOp",EDGE,"E14.44.3"),sQuery(id+"F0.wireOp",EDGE,"E14.44.4"),sQuery(id+"F0.wireOp",EDGE,"E14.44.5"),sQuery(id+"F0.wireOp",EDGE,"E14.44.6"),sQuery(id+"F0.wireOp",EDGE,"E14.44.7"),sQuery(id+"F0.wireOp",EDGE,"E14.45.0"),sQuery(id+"F0.wireOp",EDGE,"E14.45.1"),sQuery(id+"F0.wireOp",EDGE,"E14.45.2"),sQuery(id+"F0.wireOp",EDGE,"E14.45.3"),sQuery(id+"F0.wireOp",EDGE,"E14.45.4"),sQuery(id+"F0.wireOp",EDGE,"E14.45.5"),sQuery(id+"F0.wireOp",EDGE,"E14.45.6"),sQuery(id+"F0.wireOp",EDGE,"E14.45.7"),sQuery(id+"F0.wireOp",EDGE,"E14.46.0"),sQuery(id+"F0.wireOp",EDGE,"E14.46.1"),sQuery(id+"F0.wireOp",EDGE,"E14.46.2"),sQuery(id+"F0.wireOp",EDGE,"E14.46.3"),sQuery(id+"F0.wireOp",EDGE,"E14.46.4"),sQuery(id+"F0.wireOp",EDGE,"E14.46.5"),sQuery(id+"F0.wireOp",EDGE,"E14.46.6"),sQuery(id+"F0.wireOp",EDGE,"E14.46.7"),sQuery(id+"F0.wireOp",EDGE,"E14.47.0"),sQuery(id+"F0.wireOp",EDGE,"E14.47.1"),sQuery(id+"F0.wireOp",EDGE,"E14.47.2"),sQuery(id+"F0.wireOp",EDGE,"E14.47.3"),sQuery(id+"F0.wireOp",EDGE,"E14.47.4"),sQuery(id+"F0.wireOp",EDGE,"E14.47.5"),sQuery(id+"F0.wireOp",EDGE,"E14.47.6"),sQuery(id+"F0.wireOp",EDGE,"E14.47.7")])],"isStart":false});
            var sketch = newSketch(context, id + "F2", { "sketchPlane" : qUnion([Q0])});
            skCircle(sketch, "E15", {"center": v(0, 0) * mm, "radius": 22.5 * mm});
            skCircle(sketch, "E16", {"center": v(0, 0) * mm, "radius": 15 * mm});
            skSolve(sketch);
        }
        {
            var Q0;
            Q0=makeQuery(id+"F2.imprint","IMPRINT",FACE,{"disambiguationData":[TD([[makeQuery(id+"F2.imprint","IMPRINT",EDGE,{"derivedFrom":sQuery(id+"F2.wireOp",EDGE,"E16")}),1.0]])]});
            var Q1;
            Q1=makeQuery(id+"F2.imprint","IMPRINT",FACE,{"disambiguationData":[TD([[makeQuery(id+"F2.imprint","IMPRINT",EDGE,{"derivedFrom":sQuery(id+"F2.wireOp",EDGE,"E16")}),1.0]])]});
            extrude(context, id + "F3", {"entities" : qUnion([Q0, Q1]), "operationType" : NewBodyOperationType.REMOVE, "oppositeDirection" : true, "depth" : 25 * mm});
        }
        {
            var Q0;
            Q0=makeQuery(id+"F1.opExtrude","CAP_FACE",FACE,{"disambiguationData":[OSD([sQuery(id+"F0.wireOp",EDGE,"E0"),sQuery(id+"F0.wireOp",EDGE,"E4"),sQuery(id+"F0.wireOp",EDGE,"E5"),sQuery(id+"F0.wireOp",EDGE,"E6"),sQuery(id+"F0.wireOp",EDGE,"E7"),sQuery(id+"F0.wireOp",EDGE,"E9.MirrorCS"),sQuery(id+"F0.wireOp",EDGE,"E10.MirrorCS"),sQuery(id+"F0.wireOp",EDGE,"E11.MirrorCS"),sQuery(id+"F0.wireOp",EDGE,"E12.MirrorCS"),sQuery(id+"F0.wireOp",EDGE,"E14.1.0"),sQuery(id+"F0.wireOp",EDGE,"E14.1.1"),sQuery(id+"F0.wireOp",EDGE,"E14.1.2"),sQuery(id+"F0.wireOp",EDGE,"E14.1.3"),sQuery(id+"F0.wireOp",EDGE,"E14.1.4"),sQuery(id+"F0.wireOp",EDGE,"E14.1.5"),sQuery(id+"F0.wireOp",EDGE,"E14.1.6"),sQuery(id+"F0.wireOp",EDGE,"E14.1.7"),sQuery(id+"F0.wireOp",EDGE,"E14.2.0"),sQuery(id+"F0.wireOp",EDGE,"E14.2.1"),sQuery(id+"F0.wireOp",EDGE,"E14.2.2"),sQuery(id+"F0.wireOp",EDGE,"E14.2.3"),sQuery(id+"F0.wireOp",EDGE,"E14.2.4"),sQuery(id+"F0.wireOp",EDGE,"E14.2.5"),sQuery(id+"F0.wireOp",EDGE,"E14.2.6"),sQuery(id+"F0.wireOp",EDGE,"E14.2.7"),sQuery(id+"F0.wireOp",EDGE,"E14.3.0"),sQuery(id+"F0.wireOp",EDGE,"E14.3.1"),sQuery(id+"F0.wireOp",EDGE,"E14.3.2"),sQuery(id+"F0.wireOp",EDGE,"E14.3.3"),sQuery(id+"F0.wireOp",EDGE,"E14.3.4"),sQuery(id+"F0.wireOp",EDGE,"E14.3.5"),sQuery(id+"F0.wireOp",EDGE,"E14.3.6"),sQuery(id+"F0.wireOp",EDGE,"E14.3.7"),sQuery(id+"F0.wireOp",EDGE,"E14.4.0"),sQuery(id+"F0.wireOp",EDGE,"E14.4.1"),sQuery(id+"F0.wireOp",EDGE,"E14.4.2"),sQuery(id+"F0.wireOp",EDGE,"E14.4.3"),sQuery(id+"F0.wireOp",EDGE,"E14.4.4"),sQuery(id+"F0.wireOp",EDGE,"E14.4.5"),sQuery(id+"F0.wireOp",EDGE,"E14.4.6"),sQuery(id+"F0.wireOp",EDGE,"E14.4.7"),sQuery(id+"F0.wireOp",EDGE,"E14.5.0"),sQuery(id+"F0.wireOp",EDGE,"E14.5.1"),sQuery(id+"F0.wireOp",EDGE,"E14.5.2"),sQuery(id+"F0.wireOp",EDGE,"E14.5.3"),sQuery(id+"F0.wireOp",EDGE,"E14.5.4"),sQuery(id+"F0.wireOp",EDGE,"E14.5.5"),sQuery(id+"F0.wireOp",EDGE,"E14.5.6"),sQuery(id+"F0.wireOp",EDGE,"E14.5.7"),sQuery(id+"F0.wireOp",EDGE,"E14.6.0"),sQuery(id+"F0.wireOp",EDGE,"E14.6.1"),sQuery(id+"F0.wireOp",EDGE,"E14.6.2"),sQuery(id+"F0.wireOp",EDGE,"E14.6.3"),sQuery(id+"F0.wireOp",EDGE,"E14.6.4"),sQuery(id+"F0.wireOp",EDGE,"E14.6.5"),sQuery(id+"F0.wireOp",EDGE,"E14.6.6"),sQuery(id+"F0.wireOp",EDGE,"E14.6.7"),sQuery(id+"F0.wireOp",EDGE,"E14.7.0"),sQuery(id+"F0.wireOp",EDGE,"E14.7.1"),sQuery(id+"F0.wireOp",EDGE,"E14.7.2"),sQuery(id+"F0.wireOp",EDGE,"E14.7.3"),sQuery(id+"F0.wireOp",EDGE,"E14.7.4"),sQuery(id+"F0.wireOp",EDGE,"E14.7.5"),sQuery(id+"F0.wireOp",EDGE,"E14.7.6"),sQuery(id+"F0.wireOp",EDGE,"E14.7.7"),sQuery(id+"F0.wireOp",EDGE,"E14.8.0"),sQuery(id+"F0.wireOp",EDGE,"E14.8.1"),sQuery(id+"F0.wireOp",EDGE,"E14.8.2"),sQuery(id+"F0.wireOp",EDGE,"E14.8.3"),sQuery(id+"F0.wireOp",EDGE,"E14.8.4"),sQuery(id+"F0.wireOp",EDGE,"E14.8.5"),sQuery(id+"F0.wireOp",EDGE,"E14.8.6"),sQuery(id+"F0.wireOp",EDGE,"E14.8.7"),sQuery(id+"F0.wireOp",EDGE,"E14.9.0"),sQuery(id+"F0.wireOp",EDGE,"E14.9.1"),sQuery(id+"F0.wireOp",EDGE,"E14.9.2"),sQuery(id+"F0.wireOp",EDGE,"E14.9.3"),sQuery(id+"F0.wireOp",EDGE,"E14.9.4"),sQuery(id+"F0.wireOp",EDGE,"E14.9.5"),sQuery(id+"F0.wireOp",EDGE,"E14.9.6"),sQuery(id+"F0.wireOp",EDGE,"E14.9.7"),sQuery(id+"F0.wireOp",EDGE,"E14.10.0"),sQuery(id+"F0.wireOp",EDGE,"E14.10.1"),sQuery(id+"F0.wireOp",EDGE,"E14.10.2"),sQuery(id+"F0.wireOp",EDGE,"E14.10.3"),sQuery(id+"F0.wireOp",EDGE,"E14.10.4"),sQuery(id+"F0.wireOp",EDGE,"E14.10.5"),sQuery(id+"F0.wireOp",EDGE,"E14.10.6"),sQuery(id+"F0.wireOp",EDGE,"E14.10.7"),sQuery(id+"F0.wireOp",EDGE,"E14.11.0"),sQuery(id+"F0.wireOp",EDGE,"E14.11.1"),sQuery(id+"F0.wireOp",EDGE,"E14.11.2"),sQuery(id+"F0.wireOp",EDGE,"E14.11.3"),sQuery(id+"F0.wireOp",EDGE,"E14.11.4"),sQuery(id+"F0.wireOp",EDGE,"E14.11.5"),sQuery(id+"F0.wireOp",EDGE,"E14.11.6"),sQuery(id+"F0.wireOp",EDGE,"E14.11.7"),sQuery(id+"F0.wireOp",EDGE,"E14.12.0"),sQuery(id+"F0.wireOp",EDGE,"E14.12.1"),sQuery(id+"F0.wireOp",EDGE,"E14.12.2"),sQuery(id+"F0.wireOp",EDGE,"E14.12.3"),sQuery(id+"F0.wireOp",EDGE,"E14.12.4"),sQuery(id+"F0.wireOp",EDGE,"E14.12.5"),sQuery(id+"F0.wireOp",EDGE,"E14.12.6"),sQuery(id+"F0.wireOp",EDGE,"E14.12.7"),sQuery(id+"F0.wireOp",EDGE,"E14.13.0"),sQuery(id+"F0.wireOp",EDGE,"E14.13.1"),sQuery(id+"F0.wireOp",EDGE,"E14.13.2"),sQuery(id+"F0.wireOp",EDGE,"E14.13.3"),sQuery(id+"F0.wireOp",EDGE,"E14.13.4"),sQuery(id+"F0.wireOp",EDGE,"E14.13.5"),sQuery(id+"F0.wireOp",EDGE,"E14.13.6"),sQuery(id+"F0.wireOp",EDGE,"E14.13.7"),sQuery(id+"F0.wireOp",EDGE,"E14.14.0"),sQuery(id+"F0.wireOp",EDGE,"E14.14.1"),sQuery(id+"F0.wireOp",EDGE,"E14.14.2"),sQuery(id+"F0.wireOp",EDGE,"E14.14.3"),sQuery(id+"F0.wireOp",EDGE,"E14.14.4"),sQuery(id+"F0.wireOp",EDGE,"E14.14.5"),sQuery(id+"F0.wireOp",EDGE,"E14.14.6"),sQuery(id+"F0.wireOp",EDGE,"E14.14.7"),sQuery(id+"F0.wireOp",EDGE,"E14.15.0"),sQuery(id+"F0.wireOp",EDGE,"E14.15.1"),sQuery(id+"F0.wireOp",EDGE,"E14.15.2"),sQuery(id+"F0.wireOp",EDGE,"E14.15.3"),sQuery(id+"F0.wireOp",EDGE,"E14.15.4"),sQuery(id+"F0.wireOp",EDGE,"E14.15.5"),sQuery(id+"F0.wireOp",EDGE,"E14.15.6"),sQuery(id+"F0.wireOp",EDGE,"E14.15.7"),sQuery(id+"F0.wireOp",EDGE,"E14.16.0"),sQuery(id+"F0.wireOp",EDGE,"E14.16.1"),sQuery(id+"F0.wireOp",EDGE,"E14.16.2"),sQuery(id+"F0.wireOp",EDGE,"E14.16.3"),sQuery(id+"F0.wireOp",EDGE,"E14.16.4"),sQuery(id+"F0.wireOp",EDGE,"E14.16.5"),sQuery(id+"F0.wireOp",EDGE,"E14.16.6"),sQuery(id+"F0.wireOp",EDGE,"E14.16.7"),sQuery(id+"F0.wireOp",EDGE,"E14.17.0"),sQuery(id+"F0.wireOp",EDGE,"E14.17.1"),sQuery(id+"F0.wireOp",EDGE,"E14.17.2"),sQuery(id+"F0.wireOp",EDGE,"E14.17.3"),sQuery(id+"F0.wireOp",EDGE,"E14.17.4"),sQuery(id+"F0.wireOp",EDGE,"E14.17.5"),sQuery(id+"F0.wireOp",EDGE,"E14.17.6"),sQuery(id+"F0.wireOp",EDGE,"E14.17.7"),sQuery(id+"F0.wireOp",EDGE,"E14.18.0"),sQuery(id+"F0.wireOp",EDGE,"E14.18.1"),sQuery(id+"F0.wireOp",EDGE,"E14.18.2"),sQuery(id+"F0.wireOp",EDGE,"E14.18.3"),sQuery(id+"F0.wireOp",EDGE,"E14.18.4"),sQuery(id+"F0.wireOp",EDGE,"E14.18.5"),sQuery(id+"F0.wireOp",EDGE,"E14.18.6"),sQuery(id+"F0.wireOp",EDGE,"E14.18.7"),sQuery(id+"F0.wireOp",EDGE,"E14.19.0"),sQuery(id+"F0.wireOp",EDGE,"E14.19.1"),sQuery(id+"F0.wireOp",EDGE,"E14.19.2"),sQuery(id+"F0.wireOp",EDGE,"E14.19.3"),sQuery(id+"F0.wireOp",EDGE,"E14.19.4"),sQuery(id+"F0.wireOp",EDGE,"E14.19.5"),sQuery(id+"F0.wireOp",EDGE,"E14.19.6"),sQuery(id+"F0.wireOp",EDGE,"E14.19.7"),sQuery(id+"F0.wireOp",EDGE,"E14.20.0"),sQuery(id+"F0.wireOp",EDGE,"E14.20.1"),sQuery(id+"F0.wireOp",EDGE,"E14.20.2"),sQuery(id+"F0.wireOp",EDGE,"E14.20.3"),sQuery(id+"F0.wireOp",EDGE,"E14.20.4"),sQuery(id+"F0.wireOp",EDGE,"E14.20.5"),sQuery(id+"F0.wireOp",EDGE,"E14.20.6"),sQuery(id+"F0.wireOp",EDGE,"E14.20.7"),sQuery(id+"F0.wireOp",EDGE,"E14.21.0"),sQuery(id+"F0.wireOp",EDGE,"E14.21.1"),sQuery(id+"F0.wireOp",EDGE,"E14.21.2"),sQuery(id+"F0.wireOp",EDGE,"E14.21.3"),sQuery(id+"F0.wireOp",EDGE,"E14.21.4"),sQuery(id+"F0.wireOp",EDGE,"E14.21.5"),sQuery(id+"F0.wireOp",EDGE,"E14.21.6"),sQuery(id+"F0.wireOp",EDGE,"E14.21.7"),sQuery(id+"F0.wireOp",EDGE,"E14.22.0"),sQuery(id+"F0.wireOp",EDGE,"E14.22.1"),sQuery(id+"F0.wireOp",EDGE,"E14.22.2"),sQuery(id+"F0.wireOp",EDGE,"E14.22.3"),sQuery(id+"F0.wireOp",EDGE,"E14.22.4"),sQuery(id+"F0.wireOp",EDGE,"E14.22.5"),sQuery(id+"F0.wireOp",EDGE,"E14.22.6"),sQuery(id+"F0.wireOp",EDGE,"E14.22.7"),sQuery(id+"F0.wireOp",EDGE,"E14.23.0"),sQuery(id+"F0.wireOp",EDGE,"E14.23.1"),sQuery(id+"F0.wireOp",EDGE,"E14.23.2"),sQuery(id+"F0.wireOp",EDGE,"E14.23.3"),sQuery(id+"F0.wireOp",EDGE,"E14.23.4"),sQuery(id+"F0.wireOp",EDGE,"E14.23.5"),sQuery(id+"F0.wireOp",EDGE,"E14.23.6"),sQuery(id+"F0.wireOp",EDGE,"E14.23.7"),sQuery(id+"F0.wireOp",EDGE,"E14.24.0"),sQuery(id+"F0.wireOp",EDGE,"E14.24.1"),sQuery(id+"F0.wireOp",EDGE,"E14.24.2"),sQuery(id+"F0.wireOp",EDGE,"E14.24.3"),sQuery(id+"F0.wireOp",EDGE,"E14.24.4"),sQuery(id+"F0.wireOp",EDGE,"E14.24.5"),sQuery(id+"F0.wireOp",EDGE,"E14.24.6"),sQuery(id+"F0.wireOp",EDGE,"E14.24.7"),sQuery(id+"F0.wireOp",EDGE,"E14.25.0"),sQuery(id+"F0.wireOp",EDGE,"E14.25.1"),sQuery(id+"F0.wireOp",EDGE,"E14.25.2"),sQuery(id+"F0.wireOp",EDGE,"E14.25.3"),sQuery(id+"F0.wireOp",EDGE,"E14.25.4"),sQuery(id+"F0.wireOp",EDGE,"E14.25.5"),sQuery(id+"F0.wireOp",EDGE,"E14.25.6"),sQuery(id+"F0.wireOp",EDGE,"E14.25.7"),sQuery(id+"F0.wireOp",EDGE,"E14.26.0"),sQuery(id+"F0.wireOp",EDGE,"E14.26.1"),sQuery(id+"F0.wireOp",EDGE,"E14.26.2"),sQuery(id+"F0.wireOp",EDGE,"E14.26.3"),sQuery(id+"F0.wireOp",EDGE,"E14.26.4"),sQuery(id+"F0.wireOp",EDGE,"E14.26.5"),sQuery(id+"F0.wireOp",EDGE,"E14.26.6"),sQuery(id+"F0.wireOp",EDGE,"E14.26.7"),sQuery(id+"F0.wireOp",EDGE,"E14.27.0"),sQuery(id+"F0.wireOp",EDGE,"E14.27.1"),sQuery(id+"F0.wireOp",EDGE,"E14.27.2"),sQuery(id+"F0.wireOp",EDGE,"E14.27.3"),sQuery(id+"F0.wireOp",EDGE,"E14.27.4"),sQuery(id+"F0.wireOp",EDGE,"E14.27.5"),sQuery(id+"F0.wireOp",EDGE,"E14.27.6"),sQuery(id+"F0.wireOp",EDGE,"E14.27.7"),sQuery(id+"F0.wireOp",EDGE,"E14.28.0"),sQuery(id+"F0.wireOp",EDGE,"E14.28.1"),sQuery(id+"F0.wireOp",EDGE,"E14.28.2"),sQuery(id+"F0.wireOp",EDGE,"E14.28.3"),sQuery(id+"F0.wireOp",EDGE,"E14.28.4"),sQuery(id+"F0.wireOp",EDGE,"E14.28.5"),sQuery(id+"F0.wireOp",EDGE,"E14.28.6"),sQuery(id+"F0.wireOp",EDGE,"E14.28.7"),sQuery(id+"F0.wireOp",EDGE,"E14.29.0"),sQuery(id+"F0.wireOp",EDGE,"E14.29.1"),sQuery(id+"F0.wireOp",EDGE,"E14.29.2"),sQuery(id+"F0.wireOp",EDGE,"E14.29.3"),sQuery(id+"F0.wireOp",EDGE,"E14.29.4"),sQuery(id+"F0.wireOp",EDGE,"E14.29.5"),sQuery(id+"F0.wireOp",EDGE,"E14.29.6"),sQuery(id+"F0.wireOp",EDGE,"E14.29.7"),sQuery(id+"F0.wireOp",EDGE,"E14.30.0"),sQuery(id+"F0.wireOp",EDGE,"E14.30.1"),sQuery(id+"F0.wireOp",EDGE,"E14.30.2"),sQuery(id+"F0.wireOp",EDGE,"E14.30.3"),sQuery(id+"F0.wireOp",EDGE,"E14.30.4"),sQuery(id+"F0.wireOp",EDGE,"E14.30.5"),sQuery(id+"F0.wireOp",EDGE,"E14.30.6"),sQuery(id+"F0.wireOp",EDGE,"E14.30.7"),sQuery(id+"F0.wireOp",EDGE,"E14.31.0"),sQuery(id+"F0.wireOp",EDGE,"E14.31.1"),sQuery(id+"F0.wireOp",EDGE,"E14.31.2"),sQuery(id+"F0.wireOp",EDGE,"E14.31.3"),sQuery(id+"F0.wireOp",EDGE,"E14.31.4"),sQuery(id+"F0.wireOp",EDGE,"E14.31.5"),sQuery(id+"F0.wireOp",EDGE,"E14.31.6"),sQuery(id+"F0.wireOp",EDGE,"E14.31.7"),sQuery(id+"F0.wireOp",EDGE,"E14.32.0"),sQuery(id+"F0.wireOp",EDGE,"E14.32.1"),sQuery(id+"F0.wireOp",EDGE,"E14.32.2"),sQuery(id+"F0.wireOp",EDGE,"E14.32.3"),sQuery(id+"F0.wireOp",EDGE,"E14.32.4"),sQuery(id+"F0.wireOp",EDGE,"E14.32.5"),sQuery(id+"F0.wireOp",EDGE,"E14.32.6"),sQuery(id+"F0.wireOp",EDGE,"E14.32.7"),sQuery(id+"F0.wireOp",EDGE,"E14.33.0"),sQuery(id+"F0.wireOp",EDGE,"E14.33.1"),sQuery(id+"F0.wireOp",EDGE,"E14.33.2"),sQuery(id+"F0.wireOp",EDGE,"E14.33.3"),sQuery(id+"F0.wireOp",EDGE,"E14.33.4"),sQuery(id+"F0.wireOp",EDGE,"E14.33.5"),sQuery(id+"F0.wireOp",EDGE,"E14.33.6"),sQuery(id+"F0.wireOp",EDGE,"E14.33.7"),sQuery(id+"F0.wireOp",EDGE,"E14.34.0"),sQuery(id+"F0.wireOp",EDGE,"E14.34.1"),sQuery(id+"F0.wireOp",EDGE,"E14.34.2"),sQuery(id+"F0.wireOp",EDGE,"E14.34.3"),sQuery(id+"F0.wireOp",EDGE,"E14.34.4"),sQuery(id+"F0.wireOp",EDGE,"E14.34.5"),sQuery(id+"F0.wireOp",EDGE,"E14.34.6"),sQuery(id+"F0.wireOp",EDGE,"E14.34.7"),sQuery(id+"F0.wireOp",EDGE,"E14.35.0"),sQuery(id+"F0.wireOp",EDGE,"E14.35.1"),sQuery(id+"F0.wireOp",EDGE,"E14.35.2"),sQuery(id+"F0.wireOp",EDGE,"E14.35.3"),sQuery(id+"F0.wireOp",EDGE,"E14.35.4"),sQuery(id+"F0.wireOp",EDGE,"E14.35.5"),sQuery(id+"F0.wireOp",EDGE,"E14.35.6"),sQuery(id+"F0.wireOp",EDGE,"E14.35.7"),sQuery(id+"F0.wireOp",EDGE,"E14.36.0"),sQuery(id+"F0.wireOp",EDGE,"E14.36.1"),sQuery(id+"F0.wireOp",EDGE,"E14.36.2"),sQuery(id+"F0.wireOp",EDGE,"E14.36.3"),sQuery(id+"F0.wireOp",EDGE,"E14.36.4"),sQuery(id+"F0.wireOp",EDGE,"E14.36.5"),sQuery(id+"F0.wireOp",EDGE,"E14.36.6"),sQuery(id+"F0.wireOp",EDGE,"E14.36.7"),sQuery(id+"F0.wireOp",EDGE,"E14.37.0"),sQuery(id+"F0.wireOp",EDGE,"E14.37.1"),sQuery(id+"F0.wireOp",EDGE,"E14.37.2"),sQuery(id+"F0.wireOp",EDGE,"E14.37.3"),sQuery(id+"F0.wireOp",EDGE,"E14.37.4"),sQuery(id+"F0.wireOp",EDGE,"E14.37.5"),sQuery(id+"F0.wireOp",EDGE,"E14.37.6"),sQuery(id+"F0.wireOp",EDGE,"E14.37.7"),sQuery(id+"F0.wireOp",EDGE,"E14.38.0"),sQuery(id+"F0.wireOp",EDGE,"E14.38.1"),sQuery(id+"F0.wireOp",EDGE,"E14.38.2"),sQuery(id+"F0.wireOp",EDGE,"E14.38.3"),sQuery(id+"F0.wireOp",EDGE,"E14.38.4"),sQuery(id+"F0.wireOp",EDGE,"E14.38.5"),sQuery(id+"F0.wireOp",EDGE,"E14.38.6"),sQuery(id+"F0.wireOp",EDGE,"E14.38.7"),sQuery(id+"F0.wireOp",EDGE,"E14.39.0"),sQuery(id+"F0.wireOp",EDGE,"E14.39.1"),sQuery(id+"F0.wireOp",EDGE,"E14.39.2"),sQuery(id+"F0.wireOp",EDGE,"E14.39.3"),sQuery(id+"F0.wireOp",EDGE,"E14.39.4"),sQuery(id+"F0.wireOp",EDGE,"E14.39.5"),sQuery(id+"F0.wireOp",EDGE,"E14.39.6"),sQuery(id+"F0.wireOp",EDGE,"E14.39.7"),sQuery(id+"F0.wireOp",EDGE,"E14.40.0"),sQuery(id+"F0.wireOp",EDGE,"E14.40.1"),sQuery(id+"F0.wireOp",EDGE,"E14.40.2"),sQuery(id+"F0.wireOp",EDGE,"E14.40.3"),sQuery(id+"F0.wireOp",EDGE,"E14.40.4"),sQuery(id+"F0.wireOp",EDGE,"E14.40.5"),sQuery(id+"F0.wireOp",EDGE,"E14.40.6"),sQuery(id+"F0.wireOp",EDGE,"E14.40.7"),sQuery(id+"F0.wireOp",EDGE,"E14.41.0"),sQuery(id+"F0.wireOp",EDGE,"E14.41.1"),sQuery(id+"F0.wireOp",EDGE,"E14.41.2"),sQuery(id+"F0.wireOp",EDGE,"E14.41.3"),sQuery(id+"F0.wireOp",EDGE,"E14.41.4"),sQuery(id+"F0.wireOp",EDGE,"E14.41.5"),sQuery(id+"F0.wireOp",EDGE,"E14.41.6"),sQuery(id+"F0.wireOp",EDGE,"E14.41.7"),sQuery(id+"F0.wireOp",EDGE,"E14.42.0"),sQuery(id+"F0.wireOp",EDGE,"E14.42.1"),sQuery(id+"F0.wireOp",EDGE,"E14.42.2"),sQuery(id+"F0.wireOp",EDGE,"E14.42.3"),sQuery(id+"F0.wireOp",EDGE,"E14.42.4"),sQuery(id+"F0.wireOp",EDGE,"E14.42.5"),sQuery(id+"F0.wireOp",EDGE,"E14.42.6"),sQuery(id+"F0.wireOp",EDGE,"E14.42.7"),sQuery(id+"F0.wireOp",EDGE,"E14.43.0"),sQuery(id+"F0.wireOp",EDGE,"E14.43.1"),sQuery(id+"F0.wireOp",EDGE,"E14.43.2"),sQuery(id+"F0.wireOp",EDGE,"E14.43.3"),sQuery(id+"F0.wireOp",EDGE,"E14.43.4"),sQuery(id+"F0.wireOp",EDGE,"E14.43.5"),sQuery(id+"F0.wireOp",EDGE,"E14.43.6"),sQuery(id+"F0.wireOp",EDGE,"E14.43.7"),sQuery(id+"F0.wireOp",EDGE,"E14.44.0"),sQuery(id+"F0.wireOp",EDGE,"E14.44.1"),sQuery(id+"F0.wireOp",EDGE,"E14.44.2"),sQuery(id+"F0.wireOp",EDGE,"E14.44.3"),sQuery(id+"F0.wireOp",EDGE,"E14.44.4"),sQuery(id+"F0.wireOp",EDGE,"E14.44.5"),sQuery(id+"F0.wireOp",EDGE,"E14.44.6"),sQuery(id+"F0.wireOp",EDGE,"E14.44.7"),sQuery(id+"F0.wireOp",EDGE,"E14.45.0"),sQuery(id+"F0.wireOp",EDGE,"E14.45.1"),sQuery(id+"F0.wireOp",EDGE,"E14.45.2"),sQuery(id+"F0.wireOp",EDGE,"E14.45.3"),sQuery(id+"F0.wireOp",EDGE,"E14.45.4"),sQuery(id+"F0.wireOp",EDGE,"E14.45.5"),sQuery(id+"F0.wireOp",EDGE,"E14.45.6"),sQuery(id+"F0.wireOp",EDGE,"E14.45.7"),sQuery(id+"F0.wireOp",EDGE,"E14.46.0"),sQuery(id+"F0.wireOp",EDGE,"E14.46.1"),sQuery(id+"F0.wireOp",EDGE,"E14.46.2"),sQuery(id+"F0.wireOp",EDGE,"E14.46.3"),sQuery(id+"F0.wireOp",EDGE,"E14.46.4"),sQuery(id+"F0.wireOp",EDGE,"E14.46.5"),sQuery(id+"F0.wireOp",EDGE,"E14.46.6"),sQuery(id+"F0.wireOp",EDGE,"E14.46.7"),sQuery(id+"F0.wireOp",EDGE,"E14.47.0"),sQuery(id+"F0.wireOp",EDGE,"E14.47.1"),sQuery(id+"F0.wireOp",EDGE,"E14.47.2"),sQuery(id+"F0.wireOp",EDGE,"E14.47.3"),sQuery(id+"F0.wireOp",EDGE,"E14.47.4"),sQuery(id+"F0.wireOp",EDGE,"E14.47.5"),sQuery(id+"F0.wireOp",EDGE,"E14.47.6"),sQuery(id+"F0.wireOp",EDGE,"E14.47.7")])],"isStart":false});
            var sketch = newSketch(context, id + "F4", { "sketchPlane" : qUnion([Q0])});
            skCircle(sketch, "E17", {"center": v(0, 0) * mm, "radius": 56 * mm});
            skSolve(sketch);
        }
        {
            var Q0;
            Q0=makeQuery(id+"F4.imprint","IMPRINT",FACE,{"disambiguationData":[TD([[makeQuery(id+"F4.imprint","IMPRINT",EDGE,{"derivedFrom":sQuery(id+"F4.wireOp",EDGE,"E17")}),1.0]])]});
            extrude(context, id + "F5", {"entities" : qUnion([Q0]), "operationType" : NewBodyOperationType.REMOVE, "oppositeDirection" : true, "depth" : 3.5 * mm});
        }
        {
            var Q0;
            Q0=makeQuery(id+"F1.opExtrude","CAP_FACE",FACE,{"disambiguationData":[OSD([sQuery(id+"F0.wireOp",EDGE,"E0"),sQuery(id+"F0.wireOp",EDGE,"E4"),sQuery(id+"F0.wireOp",EDGE,"E5"),sQuery(id+"F0.wireOp",EDGE,"E6"),sQuery(id+"F0.wireOp",EDGE,"E7"),sQuery(id+"F0.wireOp",EDGE,"E9.MirrorCS"),sQuery(id+"F0.wireOp",EDGE,"E10.MirrorCS"),sQuery(id+"F0.wireOp",EDGE,"E11.MirrorCS"),sQuery(id+"F0.wireOp",EDGE,"E12.MirrorCS"),sQuery(id+"F0.wireOp",EDGE,"E14.1.0"),sQuery(id+"F0.wireOp",EDGE,"E14.1.1"),sQuery(id+"F0.wireOp",EDGE,"E14.1.2"),sQuery(id+"F0.wireOp",EDGE,"E14.1.3"),sQuery(id+"F0.wireOp",EDGE,"E14.1.4"),sQuery(id+"F0.wireOp",EDGE,"E14.1.5"),sQuery(id+"F0.wireOp",EDGE,"E14.1.6"),sQuery(id+"F0.wireOp",EDGE,"E14.1.7"),sQuery(id+"F0.wireOp",EDGE,"E14.2.0"),sQuery(id+"F0.wireOp",EDGE,"E14.2.1"),sQuery(id+"F0.wireOp",EDGE,"E14.2.2"),sQuery(id+"F0.wireOp",EDGE,"E14.2.3"),sQuery(id+"F0.wireOp",EDGE,"E14.2.4"),sQuery(id+"F0.wireOp",EDGE,"E14.2.5"),sQuery(id+"F0.wireOp",EDGE,"E14.2.6"),sQuery(id+"F0.wireOp",EDGE,"E14.2.7"),sQuery(id+"F0.wireOp",EDGE,"E14.3.0"),sQuery(id+"F0.wireOp",EDGE,"E14.3.1"),sQuery(id+"F0.wireOp",EDGE,"E14.3.2"),sQuery(id+"F0.wireOp",EDGE,"E14.3.3"),sQuery(id+"F0.wireOp",EDGE,"E14.3.4"),sQuery(id+"F0.wireOp",EDGE,"E14.3.5"),sQuery(id+"F0.wireOp",EDGE,"E14.3.6"),sQuery(id+"F0.wireOp",EDGE,"E14.3.7"),sQuery(id+"F0.wireOp",EDGE,"E14.4.0"),sQuery(id+"F0.wireOp",EDGE,"E14.4.1"),sQuery(id+"F0.wireOp",EDGE,"E14.4.2"),sQuery(id+"F0.wireOp",EDGE,"E14.4.3"),sQuery(id+"F0.wireOp",EDGE,"E14.4.4"),sQuery(id+"F0.wireOp",EDGE,"E14.4.5"),sQuery(id+"F0.wireOp",EDGE,"E14.4.6"),sQuery(id+"F0.wireOp",EDGE,"E14.4.7"),sQuery(id+"F0.wireOp",EDGE,"E14.5.0"),sQuery(id+"F0.wireOp",EDGE,"E14.5.1"),sQuery(id+"F0.wireOp",EDGE,"E14.5.2"),sQuery(id+"F0.wireOp",EDGE,"E14.5.3"),sQuery(id+"F0.wireOp",EDGE,"E14.5.4"),sQuery(id+"F0.wireOp",EDGE,"E14.5.5"),sQuery(id+"F0.wireOp",EDGE,"E14.5.6"),sQuery(id+"F0.wireOp",EDGE,"E14.5.7"),sQuery(id+"F0.wireOp",EDGE,"E14.6.0"),sQuery(id+"F0.wireOp",EDGE,"E14.6.1"),sQuery(id+"F0.wireOp",EDGE,"E14.6.2"),sQuery(id+"F0.wireOp",EDGE,"E14.6.3"),sQuery(id+"F0.wireOp",EDGE,"E14.6.4"),sQuery(id+"F0.wireOp",EDGE,"E14.6.5"),sQuery(id+"F0.wireOp",EDGE,"E14.6.6"),sQuery(id+"F0.wireOp",EDGE,"E14.6.7"),sQuery(id+"F0.wireOp",EDGE,"E14.7.0"),sQuery(id+"F0.wireOp",EDGE,"E14.7.1"),sQuery(id+"F0.wireOp",EDGE,"E14.7.2"),sQuery(id+"F0.wireOp",EDGE,"E14.7.3"),sQuery(id+"F0.wireOp",EDGE,"E14.7.4"),sQuery(id+"F0.wireOp",EDGE,"E14.7.5"),sQuery(id+"F0.wireOp",EDGE,"E14.7.6"),sQuery(id+"F0.wireOp",EDGE,"E14.7.7"),sQuery(id+"F0.wireOp",EDGE,"E14.8.0"),sQuery(id+"F0.wireOp",EDGE,"E14.8.1"),sQuery(id+"F0.wireOp",EDGE,"E14.8.2"),sQuery(id+"F0.wireOp",EDGE,"E14.8.3"),sQuery(id+"F0.wireOp",EDGE,"E14.8.4"),sQuery(id+"F0.wireOp",EDGE,"E14.8.5"),sQuery(id+"F0.wireOp",EDGE,"E14.8.6"),sQuery(id+"F0.wireOp",EDGE,"E14.8.7"),sQuery(id+"F0.wireOp",EDGE,"E14.9.0"),sQuery(id+"F0.wireOp",EDGE,"E14.9.1"),sQuery(id+"F0.wireOp",EDGE,"E14.9.2"),sQuery(id+"F0.wireOp",EDGE,"E14.9.3"),sQuery(id+"F0.wireOp",EDGE,"E14.9.4"),sQuery(id+"F0.wireOp",EDGE,"E14.9.5"),sQuery(id+"F0.wireOp",EDGE,"E14.9.6"),sQuery(id+"F0.wireOp",EDGE,"E14.9.7"),sQuery(id+"F0.wireOp",EDGE,"E14.10.0"),sQuery(id+"F0.wireOp",EDGE,"E14.10.1"),sQuery(id+"F0.wireOp",EDGE,"E14.10.2"),sQuery(id+"F0.wireOp",EDGE,"E14.10.3"),sQuery(id+"F0.wireOp",EDGE,"E14.10.4"),sQuery(id+"F0.wireOp",EDGE,"E14.10.5"),sQuery(id+"F0.wireOp",EDGE,"E14.10.6"),sQuery(id+"F0.wireOp",EDGE,"E14.10.7"),sQuery(id+"F0.wireOp",EDGE,"E14.11.0"),sQuery(id+"F0.wireOp",EDGE,"E14.11.1"),sQuery(id+"F0.wireOp",EDGE,"E14.11.2"),sQuery(id+"F0.wireOp",EDGE,"E14.11.3"),sQuery(id+"F0.wireOp",EDGE,"E14.11.4"),sQuery(id+"F0.wireOp",EDGE,"E14.11.5"),sQuery(id+"F0.wireOp",EDGE,"E14.11.6"),sQuery(id+"F0.wireOp",EDGE,"E14.11.7"),sQuery(id+"F0.wireOp",EDGE,"E14.12.0"),sQuery(id+"F0.wireOp",EDGE,"E14.12.1"),sQuery(id+"F0.wireOp",EDGE,"E14.12.2"),sQuery(id+"F0.wireOp",EDGE,"E14.12.3"),sQuery(id+"F0.wireOp",EDGE,"E14.12.4"),sQuery(id+"F0.wireOp",EDGE,"E14.12.5"),sQuery(id+"F0.wireOp",EDGE,"E14.12.6"),sQuery(id+"F0.wireOp",EDGE,"E14.12.7"),sQuery(id+"F0.wireOp",EDGE,"E14.13.0"),sQuery(id+"F0.wireOp",EDGE,"E14.13.1"),sQuery(id+"F0.wireOp",EDGE,"E14.13.2"),sQuery(id+"F0.wireOp",EDGE,"E14.13.3"),sQuery(id+"F0.wireOp",EDGE,"E14.13.4"),sQuery(id+"F0.wireOp",EDGE,"E14.13.5"),sQuery(id+"F0.wireOp",EDGE,"E14.13.6"),sQuery(id+"F0.wireOp",EDGE,"E14.13.7"),sQuery(id+"F0.wireOp",EDGE,"E14.14.0"),sQuery(id+"F0.wireOp",EDGE,"E14.14.1"),sQuery(id+"F0.wireOp",EDGE,"E14.14.2"),sQuery(id+"F0.wireOp",EDGE,"E14.14.3"),sQuery(id+"F0.wireOp",EDGE,"E14.14.4"),sQuery(id+"F0.wireOp",EDGE,"E14.14.5"),sQuery(id+"F0.wireOp",EDGE,"E14.14.6"),sQuery(id+"F0.wireOp",EDGE,"E14.14.7"),sQuery(id+"F0.wireOp",EDGE,"E14.15.0"),sQuery(id+"F0.wireOp",EDGE,"E14.15.1"),sQuery(id+"F0.wireOp",EDGE,"E14.15.2"),sQuery(id+"F0.wireOp",EDGE,"E14.15.3"),sQuery(id+"F0.wireOp",EDGE,"E14.15.4"),sQuery(id+"F0.wireOp",EDGE,"E14.15.5"),sQuery(id+"F0.wireOp",EDGE,"E14.15.6"),sQuery(id+"F0.wireOp",EDGE,"E14.15.7"),sQuery(id+"F0.wireOp",EDGE,"E14.16.0"),sQuery(id+"F0.wireOp",EDGE,"E14.16.1"),sQuery(id+"F0.wireOp",EDGE,"E14.16.2"),sQuery(id+"F0.wireOp",EDGE,"E14.16.3"),sQuery(id+"F0.wireOp",EDGE,"E14.16.4"),sQuery(id+"F0.wireOp",EDGE,"E14.16.5"),sQuery(id+"F0.wireOp",EDGE,"E14.16.6"),sQuery(id+"F0.wireOp",EDGE,"E14.16.7"),sQuery(id+"F0.wireOp",EDGE,"E14.17.0"),sQuery(id+"F0.wireOp",EDGE,"E14.17.1"),sQuery(id+"F0.wireOp",EDGE,"E14.17.2"),sQuery(id+"F0.wireOp",EDGE,"E14.17.3"),sQuery(id+"F0.wireOp",EDGE,"E14.17.4"),sQuery(id+"F0.wireOp",EDGE,"E14.17.5"),sQuery(id+"F0.wireOp",EDGE,"E14.17.6"),sQuery(id+"F0.wireOp",EDGE,"E14.17.7"),sQuery(id+"F0.wireOp",EDGE,"E14.18.0"),sQuery(id+"F0.wireOp",EDGE,"E14.18.1"),sQuery(id+"F0.wireOp",EDGE,"E14.18.2"),sQuery(id+"F0.wireOp",EDGE,"E14.18.3"),sQuery(id+"F0.wireOp",EDGE,"E14.18.4"),sQuery(id+"F0.wireOp",EDGE,"E14.18.5"),sQuery(id+"F0.wireOp",EDGE,"E14.18.6"),sQuery(id+"F0.wireOp",EDGE,"E14.18.7"),sQuery(id+"F0.wireOp",EDGE,"E14.19.0"),sQuery(id+"F0.wireOp",EDGE,"E14.19.1"),sQuery(id+"F0.wireOp",EDGE,"E14.19.2"),sQuery(id+"F0.wireOp",EDGE,"E14.19.3"),sQuery(id+"F0.wireOp",EDGE,"E14.19.4"),sQuery(id+"F0.wireOp",EDGE,"E14.19.5"),sQuery(id+"F0.wireOp",EDGE,"E14.19.6"),sQuery(id+"F0.wireOp",EDGE,"E14.19.7"),sQuery(id+"F0.wireOp",EDGE,"E14.20.0"),sQuery(id+"F0.wireOp",EDGE,"E14.20.1"),sQuery(id+"F0.wireOp",EDGE,"E14.20.2"),sQuery(id+"F0.wireOp",EDGE,"E14.20.3"),sQuery(id+"F0.wireOp",EDGE,"E14.20.4"),sQuery(id+"F0.wireOp",EDGE,"E14.20.5"),sQuery(id+"F0.wireOp",EDGE,"E14.20.6"),sQuery(id+"F0.wireOp",EDGE,"E14.20.7"),sQuery(id+"F0.wireOp",EDGE,"E14.21.0"),sQuery(id+"F0.wireOp",EDGE,"E14.21.1"),sQuery(id+"F0.wireOp",EDGE,"E14.21.2"),sQuery(id+"F0.wireOp",EDGE,"E14.21.3"),sQuery(id+"F0.wireOp",EDGE,"E14.21.4"),sQuery(id+"F0.wireOp",EDGE,"E14.21.5"),sQuery(id+"F0.wireOp",EDGE,"E14.21.6"),sQuery(id+"F0.wireOp",EDGE,"E14.21.7"),sQuery(id+"F0.wireOp",EDGE,"E14.22.0"),sQuery(id+"F0.wireOp",EDGE,"E14.22.1"),sQuery(id+"F0.wireOp",EDGE,"E14.22.2"),sQuery(id+"F0.wireOp",EDGE,"E14.22.3"),sQuery(id+"F0.wireOp",EDGE,"E14.22.4"),sQuery(id+"F0.wireOp",EDGE,"E14.22.5"),sQuery(id+"F0.wireOp",EDGE,"E14.22.6"),sQuery(id+"F0.wireOp",EDGE,"E14.22.7"),sQuery(id+"F0.wireOp",EDGE,"E14.23.0"),sQuery(id+"F0.wireOp",EDGE,"E14.23.1"),sQuery(id+"F0.wireOp",EDGE,"E14.23.2"),sQuery(id+"F0.wireOp",EDGE,"E14.23.3"),sQuery(id+"F0.wireOp",EDGE,"E14.23.4"),sQuery(id+"F0.wireOp",EDGE,"E14.23.5"),sQuery(id+"F0.wireOp",EDGE,"E14.23.6"),sQuery(id+"F0.wireOp",EDGE,"E14.23.7"),sQuery(id+"F0.wireOp",EDGE,"E14.24.0"),sQuery(id+"F0.wireOp",EDGE,"E14.24.1"),sQuery(id+"F0.wireOp",EDGE,"E14.24.2"),sQuery(id+"F0.wireOp",EDGE,"E14.24.3"),sQuery(id+"F0.wireOp",EDGE,"E14.24.4"),sQuery(id+"F0.wireOp",EDGE,"E14.24.5"),sQuery(id+"F0.wireOp",EDGE,"E14.24.6"),sQuery(id+"F0.wireOp",EDGE,"E14.24.7"),sQuery(id+"F0.wireOp",EDGE,"E14.25.0"),sQuery(id+"F0.wireOp",EDGE,"E14.25.1"),sQuery(id+"F0.wireOp",EDGE,"E14.25.2"),sQuery(id+"F0.wireOp",EDGE,"E14.25.3"),sQuery(id+"F0.wireOp",EDGE,"E14.25.4"),sQuery(id+"F0.wireOp",EDGE,"E14.25.5"),sQuery(id+"F0.wireOp",EDGE,"E14.25.6"),sQuery(id+"F0.wireOp",EDGE,"E14.25.7"),sQuery(id+"F0.wireOp",EDGE,"E14.26.0"),sQuery(id+"F0.wireOp",EDGE,"E14.26.1"),sQuery(id+"F0.wireOp",EDGE,"E14.26.2"),sQuery(id+"F0.wireOp",EDGE,"E14.26.3"),sQuery(id+"F0.wireOp",EDGE,"E14.26.4"),sQuery(id+"F0.wireOp",EDGE,"E14.26.5"),sQuery(id+"F0.wireOp",EDGE,"E14.26.6"),sQuery(id+"F0.wireOp",EDGE,"E14.26.7"),sQuery(id+"F0.wireOp",EDGE,"E14.27.0"),sQuery(id+"F0.wireOp",EDGE,"E14.27.1"),sQuery(id+"F0.wireOp",EDGE,"E14.27.2"),sQuery(id+"F0.wireOp",EDGE,"E14.27.3"),sQuery(id+"F0.wireOp",EDGE,"E14.27.4"),sQuery(id+"F0.wireOp",EDGE,"E14.27.5"),sQuery(id+"F0.wireOp",EDGE,"E14.27.6"),sQuery(id+"F0.wireOp",EDGE,"E14.27.7"),sQuery(id+"F0.wireOp",EDGE,"E14.28.0"),sQuery(id+"F0.wireOp",EDGE,"E14.28.1"),sQuery(id+"F0.wireOp",EDGE,"E14.28.2"),sQuery(id+"F0.wireOp",EDGE,"E14.28.3"),sQuery(id+"F0.wireOp",EDGE,"E14.28.4"),sQuery(id+"F0.wireOp",EDGE,"E14.28.5"),sQuery(id+"F0.wireOp",EDGE,"E14.28.6"),sQuery(id+"F0.wireOp",EDGE,"E14.28.7"),sQuery(id+"F0.wireOp",EDGE,"E14.29.0"),sQuery(id+"F0.wireOp",EDGE,"E14.29.1"),sQuery(id+"F0.wireOp",EDGE,"E14.29.2"),sQuery(id+"F0.wireOp",EDGE,"E14.29.3"),sQuery(id+"F0.wireOp",EDGE,"E14.29.4"),sQuery(id+"F0.wireOp",EDGE,"E14.29.5"),sQuery(id+"F0.wireOp",EDGE,"E14.29.6"),sQuery(id+"F0.wireOp",EDGE,"E14.29.7"),sQuery(id+"F0.wireOp",EDGE,"E14.30.0"),sQuery(id+"F0.wireOp",EDGE,"E14.30.1"),sQuery(id+"F0.wireOp",EDGE,"E14.30.2"),sQuery(id+"F0.wireOp",EDGE,"E14.30.3"),sQuery(id+"F0.wireOp",EDGE,"E14.30.4"),sQuery(id+"F0.wireOp",EDGE,"E14.30.5"),sQuery(id+"F0.wireOp",EDGE,"E14.30.6"),sQuery(id+"F0.wireOp",EDGE,"E14.30.7"),sQuery(id+"F0.wireOp",EDGE,"E14.31.0"),sQuery(id+"F0.wireOp",EDGE,"E14.31.1"),sQuery(id+"F0.wireOp",EDGE,"E14.31.2"),sQuery(id+"F0.wireOp",EDGE,"E14.31.3"),sQuery(id+"F0.wireOp",EDGE,"E14.31.4"),sQuery(id+"F0.wireOp",EDGE,"E14.31.5"),sQuery(id+"F0.wireOp",EDGE,"E14.31.6"),sQuery(id+"F0.wireOp",EDGE,"E14.31.7"),sQuery(id+"F0.wireOp",EDGE,"E14.32.0"),sQuery(id+"F0.wireOp",EDGE,"E14.32.1"),sQuery(id+"F0.wireOp",EDGE,"E14.32.2"),sQuery(id+"F0.wireOp",EDGE,"E14.32.3"),sQuery(id+"F0.wireOp",EDGE,"E14.32.4"),sQuery(id+"F0.wireOp",EDGE,"E14.32.5"),sQuery(id+"F0.wireOp",EDGE,"E14.32.6"),sQuery(id+"F0.wireOp",EDGE,"E14.32.7"),sQuery(id+"F0.wireOp",EDGE,"E14.33.0"),sQuery(id+"F0.wireOp",EDGE,"E14.33.1"),sQuery(id+"F0.wireOp",EDGE,"E14.33.2"),sQuery(id+"F0.wireOp",EDGE,"E14.33.3"),sQuery(id+"F0.wireOp",EDGE,"E14.33.4"),sQuery(id+"F0.wireOp",EDGE,"E14.33.5"),sQuery(id+"F0.wireOp",EDGE,"E14.33.6"),sQuery(id+"F0.wireOp",EDGE,"E14.33.7"),sQuery(id+"F0.wireOp",EDGE,"E14.34.0"),sQuery(id+"F0.wireOp",EDGE,"E14.34.1"),sQuery(id+"F0.wireOp",EDGE,"E14.34.2"),sQuery(id+"F0.wireOp",EDGE,"E14.34.3"),sQuery(id+"F0.wireOp",EDGE,"E14.34.4"),sQuery(id+"F0.wireOp",EDGE,"E14.34.5"),sQuery(id+"F0.wireOp",EDGE,"E14.34.6"),sQuery(id+"F0.wireOp",EDGE,"E14.34.7"),sQuery(id+"F0.wireOp",EDGE,"E14.35.0"),sQuery(id+"F0.wireOp",EDGE,"E14.35.1"),sQuery(id+"F0.wireOp",EDGE,"E14.35.2"),sQuery(id+"F0.wireOp",EDGE,"E14.35.3"),sQuery(id+"F0.wireOp",EDGE,"E14.35.4"),sQuery(id+"F0.wireOp",EDGE,"E14.35.5"),sQuery(id+"F0.wireOp",EDGE,"E14.35.6"),sQuery(id+"F0.wireOp",EDGE,"E14.35.7"),sQuery(id+"F0.wireOp",EDGE,"E14.36.0"),sQuery(id+"F0.wireOp",EDGE,"E14.36.1"),sQuery(id+"F0.wireOp",EDGE,"E14.36.2"),sQuery(id+"F0.wireOp",EDGE,"E14.36.3"),sQuery(id+"F0.wireOp",EDGE,"E14.36.4"),sQuery(id+"F0.wireOp",EDGE,"E14.36.5"),sQuery(id+"F0.wireOp",EDGE,"E14.36.6"),sQuery(id+"F0.wireOp",EDGE,"E14.36.7"),sQuery(id+"F0.wireOp",EDGE,"E14.37.0"),sQuery(id+"F0.wireOp",EDGE,"E14.37.1"),sQuery(id+"F0.wireOp",EDGE,"E14.37.2"),sQuery(id+"F0.wireOp",EDGE,"E14.37.3"),sQuery(id+"F0.wireOp",EDGE,"E14.37.4"),sQuery(id+"F0.wireOp",EDGE,"E14.37.5"),sQuery(id+"F0.wireOp",EDGE,"E14.37.6"),sQuery(id+"F0.wireOp",EDGE,"E14.37.7"),sQuery(id+"F0.wireOp",EDGE,"E14.38.0"),sQuery(id+"F0.wireOp",EDGE,"E14.38.1"),sQuery(id+"F0.wireOp",EDGE,"E14.38.2"),sQuery(id+"F0.wireOp",EDGE,"E14.38.3"),sQuery(id+"F0.wireOp",EDGE,"E14.38.4"),sQuery(id+"F0.wireOp",EDGE,"E14.38.5"),sQuery(id+"F0.wireOp",EDGE,"E14.38.6"),sQuery(id+"F0.wireOp",EDGE,"E14.38.7"),sQuery(id+"F0.wireOp",EDGE,"E14.39.0"),sQuery(id+"F0.wireOp",EDGE,"E14.39.1"),sQuery(id+"F0.wireOp",EDGE,"E14.39.2"),sQuery(id+"F0.wireOp",EDGE,"E14.39.3"),sQuery(id+"F0.wireOp",EDGE,"E14.39.4"),sQuery(id+"F0.wireOp",EDGE,"E14.39.5"),sQuery(id+"F0.wireOp",EDGE,"E14.39.6"),sQuery(id+"F0.wireOp",EDGE,"E14.39.7"),sQuery(id+"F0.wireOp",EDGE,"E14.40.0"),sQuery(id+"F0.wireOp",EDGE,"E14.40.1"),sQuery(id+"F0.wireOp",EDGE,"E14.40.2"),sQuery(id+"F0.wireOp",EDGE,"E14.40.3"),sQuery(id+"F0.wireOp",EDGE,"E14.40.4"),sQuery(id+"F0.wireOp",EDGE,"E14.40.5"),sQuery(id+"F0.wireOp",EDGE,"E14.40.6"),sQuery(id+"F0.wireOp",EDGE,"E14.40.7"),sQuery(id+"F0.wireOp",EDGE,"E14.41.0"),sQuery(id+"F0.wireOp",EDGE,"E14.41.1"),sQuery(id+"F0.wireOp",EDGE,"E14.41.2"),sQuery(id+"F0.wireOp",EDGE,"E14.41.3"),sQuery(id+"F0.wireOp",EDGE,"E14.41.4"),sQuery(id+"F0.wireOp",EDGE,"E14.41.5"),sQuery(id+"F0.wireOp",EDGE,"E14.41.6"),sQuery(id+"F0.wireOp",EDGE,"E14.41.7"),sQuery(id+"F0.wireOp",EDGE,"E14.42.0"),sQuery(id+"F0.wireOp",EDGE,"E14.42.1"),sQuery(id+"F0.wireOp",EDGE,"E14.42.2"),sQuery(id+"F0.wireOp",EDGE,"E14.42.3"),sQuery(id+"F0.wireOp",EDGE,"E14.42.4"),sQuery(id+"F0.wireOp",EDGE,"E14.42.5"),sQuery(id+"F0.wireOp",EDGE,"E14.42.6"),sQuery(id+"F0.wireOp",EDGE,"E14.42.7"),sQuery(id+"F0.wireOp",EDGE,"E14.43.0"),sQuery(id+"F0.wireOp",EDGE,"E14.43.1"),sQuery(id+"F0.wireOp",EDGE,"E14.43.2"),sQuery(id+"F0.wireOp",EDGE,"E14.43.3"),sQuery(id+"F0.wireOp",EDGE,"E14.43.4"),sQuery(id+"F0.wireOp",EDGE,"E14.43.5"),sQuery(id+"F0.wireOp",EDGE,"E14.43.6"),sQuery(id+"F0.wireOp",EDGE,"E14.43.7"),sQuery(id+"F0.wireOp",EDGE,"E14.44.0"),sQuery(id+"F0.wireOp",EDGE,"E14.44.1"),sQuery(id+"F0.wireOp",EDGE,"E14.44.2"),sQuery(id+"F0.wireOp",EDGE,"E14.44.3"),sQuery(id+"F0.wireOp",EDGE,"E14.44.4"),sQuery(id+"F0.wireOp",EDGE,"E14.44.5"),sQuery(id+"F0.wireOp",EDGE,"E14.44.6"),sQuery(id+"F0.wireOp",EDGE,"E14.44.7"),sQuery(id+"F0.wireOp",EDGE,"E14.45.0"),sQuery(id+"F0.wireOp",EDGE,"E14.45.1"),sQuery(id+"F0.wireOp",EDGE,"E14.45.2"),sQuery(id+"F0.wireOp",EDGE,"E14.45.3"),sQuery(id+"F0.wireOp",EDGE,"E14.45.4"),sQuery(id+"F0.wireOp",EDGE,"E14.45.5"),sQuery(id+"F0.wireOp",EDGE,"E14.45.6"),sQuery(id+"F0.wireOp",EDGE,"E14.45.7"),sQuery(id+"F0.wireOp",EDGE,"E14.46.0"),sQuery(id+"F0.wireOp",EDGE,"E14.46.1"),sQuery(id+"F0.wireOp",EDGE,"E14.46.2"),sQuery(id+"F0.wireOp",EDGE,"E14.46.3"),sQuery(id+"F0.wireOp",EDGE,"E14.46.4"),sQuery(id+"F0.wireOp",EDGE,"E14.46.5"),sQuery(id+"F0.wireOp",EDGE,"E14.46.6"),sQuery(id+"F0.wireOp",EDGE,"E14.46.7"),sQuery(id+"F0.wireOp",EDGE,"E14.47.0"),sQuery(id+"F0.wireOp",EDGE,"E14.47.1"),sQuery(id+"F0.wireOp",EDGE,"E14.47.2"),sQuery(id+"F0.wireOp",EDGE,"E14.47.3"),sQuery(id+"F0.wireOp",EDGE,"E14.47.4"),sQuery(id+"F0.wireOp",EDGE,"E14.47.5"),sQuery(id+"F0.wireOp",EDGE,"E14.47.6"),sQuery(id+"F0.wireOp",EDGE,"E14.47.7")])],"isStart":true});
            var sketch = newSketch(context, id + "F6", { "sketchPlane" : qUnion([Q0])});
            skCircle(sketch, "E18", {"center": v(0, 0) * mm, "radius": 56 * mm});
            skSolve(sketch);
        }
        {
            var Q0;
            Q0=makeQuery(id+"F6.imprint","IMPRINT",FACE,{"disambiguationData":[TD([[makeQuery(id+"F6.imprint","IMPRINT",EDGE,{"derivedFrom":sQuery(id+"F6.wireOp",EDGE,"E18")}),1.0]])]});
            extrude(context, id + "F7", {"entities" : qUnion([Q0]), "operationType" : NewBodyOperationType.REMOVE, "oppositeDirection" : true, "depth" : 3.5 * mm});
        }
        {
            var Q0;
            Q0=makeQuery(id+"F1.opExtrude","CAP_FACE",FACE,{"disambiguationData":[OSD([sQuery(id+"F0.wireOp",EDGE,"E0"),sQuery(id+"F0.wireOp",EDGE,"E4"),sQuery(id+"F0.wireOp",EDGE,"E5"),sQuery(id+"F0.wireOp",EDGE,"E6"),sQuery(id+"F0.wireOp",EDGE,"E7"),sQuery(id+"F0.wireOp",EDGE,"E9.MirrorCS"),sQuery(id+"F0.wireOp",EDGE,"E10.MirrorCS"),sQuery(id+"F0.wireOp",EDGE,"E11.MirrorCS"),sQuery(id+"F0.wireOp",EDGE,"E12.MirrorCS"),sQuery(id+"F0.wireOp",EDGE,"E14.1.0"),sQuery(id+"F0.wireOp",EDGE,"E14.1.1"),sQuery(id+"F0.wireOp",EDGE,"E14.1.2"),sQuery(id+"F0.wireOp",EDGE,"E14.1.3"),sQuery(id+"F0.wireOp",EDGE,"E14.1.4"),sQuery(id+"F0.wireOp",EDGE,"E14.1.5"),sQuery(id+"F0.wireOp",EDGE,"E14.1.6"),sQuery(id+"F0.wireOp",EDGE,"E14.1.7"),sQuery(id+"F0.wireOp",EDGE,"E14.2.0"),sQuery(id+"F0.wireOp",EDGE,"E14.2.1"),sQuery(id+"F0.wireOp",EDGE,"E14.2.2"),sQuery(id+"F0.wireOp",EDGE,"E14.2.3"),sQuery(id+"F0.wireOp",EDGE,"E14.2.4"),sQuery(id+"F0.wireOp",EDGE,"E14.2.5"),sQuery(id+"F0.wireOp",EDGE,"E14.2.6"),sQuery(id+"F0.wireOp",EDGE,"E14.2.7"),sQuery(id+"F0.wireOp",EDGE,"E14.3.0"),sQuery(id+"F0.wireOp",EDGE,"E14.3.1"),sQuery(id+"F0.wireOp",EDGE,"E14.3.2"),sQuery(id+"F0.wireOp",EDGE,"E14.3.3"),sQuery(id+"F0.wireOp",EDGE,"E14.3.4"),sQuery(id+"F0.wireOp",EDGE,"E14.3.5"),sQuery(id+"F0.wireOp",EDGE,"E14.3.6"),sQuery(id+"F0.wireOp",EDGE,"E14.3.7"),sQuery(id+"F0.wireOp",EDGE,"E14.4.0"),sQuery(id+"F0.wireOp",EDGE,"E14.4.1"),sQuery(id+"F0.wireOp",EDGE,"E14.4.2"),sQuery(id+"F0.wireOp",EDGE,"E14.4.3"),sQuery(id+"F0.wireOp",EDGE,"E14.4.4"),sQuery(id+"F0.wireOp",EDGE,"E14.4.5"),sQuery(id+"F0.wireOp",EDGE,"E14.4.6"),sQuery(id+"F0.wireOp",EDGE,"E14.4.7"),sQuery(id+"F0.wireOp",EDGE,"E14.5.0"),sQuery(id+"F0.wireOp",EDGE,"E14.5.1"),sQuery(id+"F0.wireOp",EDGE,"E14.5.2"),sQuery(id+"F0.wireOp",EDGE,"E14.5.3"),sQuery(id+"F0.wireOp",EDGE,"E14.5.4"),sQuery(id+"F0.wireOp",EDGE,"E14.5.5"),sQuery(id+"F0.wireOp",EDGE,"E14.5.6"),sQuery(id+"F0.wireOp",EDGE,"E14.5.7"),sQuery(id+"F0.wireOp",EDGE,"E14.6.0"),sQuery(id+"F0.wireOp",EDGE,"E14.6.1"),sQuery(id+"F0.wireOp",EDGE,"E14.6.2"),sQuery(id+"F0.wireOp",EDGE,"E14.6.3"),sQuery(id+"F0.wireOp",EDGE,"E14.6.4"),sQuery(id+"F0.wireOp",EDGE,"E14.6.5"),sQuery(id+"F0.wireOp",EDGE,"E14.6.6"),sQuery(id+"F0.wireOp",EDGE,"E14.6.7"),sQuery(id+"F0.wireOp",EDGE,"E14.7.0"),sQuery(id+"F0.wireOp",EDGE,"E14.7.1"),sQuery(id+"F0.wireOp",EDGE,"E14.7.2"),sQuery(id+"F0.wireOp",EDGE,"E14.7.3"),sQuery(id+"F0.wireOp",EDGE,"E14.7.4"),sQuery(id+"F0.wireOp",EDGE,"E14.7.5"),sQuery(id+"F0.wireOp",EDGE,"E14.7.6"),sQuery(id+"F0.wireOp",EDGE,"E14.7.7"),sQuery(id+"F0.wireOp",EDGE,"E14.8.0"),sQuery(id+"F0.wireOp",EDGE,"E14.8.1"),sQuery(id+"F0.wireOp",EDGE,"E14.8.2"),sQuery(id+"F0.wireOp",EDGE,"E14.8.3"),sQuery(id+"F0.wireOp",EDGE,"E14.8.4"),sQuery(id+"F0.wireOp",EDGE,"E14.8.5"),sQuery(id+"F0.wireOp",EDGE,"E14.8.6"),sQuery(id+"F0.wireOp",EDGE,"E14.8.7"),sQuery(id+"F0.wireOp",EDGE,"E14.9.0"),sQuery(id+"F0.wireOp",EDGE,"E14.9.1"),sQuery(id+"F0.wireOp",EDGE,"E14.9.2"),sQuery(id+"F0.wireOp",EDGE,"E14.9.3"),sQuery(id+"F0.wireOp",EDGE,"E14.9.4"),sQuery(id+"F0.wireOp",EDGE,"E14.9.5"),sQuery(id+"F0.wireOp",EDGE,"E14.9.6"),sQuery(id+"F0.wireOp",EDGE,"E14.9.7"),sQuery(id+"F0.wireOp",EDGE,"E14.10.0"),sQuery(id+"F0.wireOp",EDGE,"E14.10.1"),sQuery(id+"F0.wireOp",EDGE,"E14.10.2"),sQuery(id+"F0.wireOp",EDGE,"E14.10.3"),sQuery(id+"F0.wireOp",EDGE,"E14.10.4"),sQuery(id+"F0.wireOp",EDGE,"E14.10.5"),sQuery(id+"F0.wireOp",EDGE,"E14.10.6"),sQuery(id+"F0.wireOp",EDGE,"E14.10.7"),sQuery(id+"F0.wireOp",EDGE,"E14.11.0"),sQuery(id+"F0.wireOp",EDGE,"E14.11.1"),sQuery(id+"F0.wireOp",EDGE,"E14.11.2"),sQuery(id+"F0.wireOp",EDGE,"E14.11.3"),sQuery(id+"F0.wireOp",EDGE,"E14.11.4"),sQuery(id+"F0.wireOp",EDGE,"E14.11.5"),sQuery(id+"F0.wireOp",EDGE,"E14.11.6"),sQuery(id+"F0.wireOp",EDGE,"E14.11.7"),sQuery(id+"F0.wireOp",EDGE,"E14.12.0"),sQuery(id+"F0.wireOp",EDGE,"E14.12.1"),sQuery(id+"F0.wireOp",EDGE,"E14.12.2"),sQuery(id+"F0.wireOp",EDGE,"E14.12.3"),sQuery(id+"F0.wireOp",EDGE,"E14.12.4"),sQuery(id+"F0.wireOp",EDGE,"E14.12.5"),sQuery(id+"F0.wireOp",EDGE,"E14.12.6"),sQuery(id+"F0.wireOp",EDGE,"E14.12.7"),sQuery(id+"F0.wireOp",EDGE,"E14.13.0"),sQuery(id+"F0.wireOp",EDGE,"E14.13.1"),sQuery(id+"F0.wireOp",EDGE,"E14.13.2"),sQuery(id+"F0.wireOp",EDGE,"E14.13.3"),sQuery(id+"F0.wireOp",EDGE,"E14.13.4"),sQuery(id+"F0.wireOp",EDGE,"E14.13.5"),sQuery(id+"F0.wireOp",EDGE,"E14.13.6"),sQuery(id+"F0.wireOp",EDGE,"E14.13.7"),sQuery(id+"F0.wireOp",EDGE,"E14.14.0"),sQuery(id+"F0.wireOp",EDGE,"E14.14.1"),sQuery(id+"F0.wireOp",EDGE,"E14.14.2"),sQuery(id+"F0.wireOp",EDGE,"E14.14.3"),sQuery(id+"F0.wireOp",EDGE,"E14.14.4"),sQuery(id+"F0.wireOp",EDGE,"E14.14.5"),sQuery(id+"F0.wireOp",EDGE,"E14.14.6"),sQuery(id+"F0.wireOp",EDGE,"E14.14.7"),sQuery(id+"F0.wireOp",EDGE,"E14.15.0"),sQuery(id+"F0.wireOp",EDGE,"E14.15.1"),sQuery(id+"F0.wireOp",EDGE,"E14.15.2"),sQuery(id+"F0.wireOp",EDGE,"E14.15.3"),sQuery(id+"F0.wireOp",EDGE,"E14.15.4"),sQuery(id+"F0.wireOp",EDGE,"E14.15.5"),sQuery(id+"F0.wireOp",EDGE,"E14.15.6"),sQuery(id+"F0.wireOp",EDGE,"E14.15.7"),sQuery(id+"F0.wireOp",EDGE,"E14.16.0"),sQuery(id+"F0.wireOp",EDGE,"E14.16.1"),sQuery(id+"F0.wireOp",EDGE,"E14.16.2"),sQuery(id+"F0.wireOp",EDGE,"E14.16.3"),sQuery(id+"F0.wireOp",EDGE,"E14.16.4"),sQuery(id+"F0.wireOp",EDGE,"E14.16.5"),sQuery(id+"F0.wireOp",EDGE,"E14.16.6"),sQuery(id+"F0.wireOp",EDGE,"E14.16.7"),sQuery(id+"F0.wireOp",EDGE,"E14.17.0"),sQuery(id+"F0.wireOp",EDGE,"E14.17.1"),sQuery(id+"F0.wireOp",EDGE,"E14.17.2"),sQuery(id+"F0.wireOp",EDGE,"E14.17.3"),sQuery(id+"F0.wireOp",EDGE,"E14.17.4"),sQuery(id+"F0.wireOp",EDGE,"E14.17.5"),sQuery(id+"F0.wireOp",EDGE,"E14.17.6"),sQuery(id+"F0.wireOp",EDGE,"E14.17.7"),sQuery(id+"F0.wireOp",EDGE,"E14.18.0"),sQuery(id+"F0.wireOp",EDGE,"E14.18.1"),sQuery(id+"F0.wireOp",EDGE,"E14.18.2"),sQuery(id+"F0.wireOp",EDGE,"E14.18.3"),sQuery(id+"F0.wireOp",EDGE,"E14.18.4"),sQuery(id+"F0.wireOp",EDGE,"E14.18.5"),sQuery(id+"F0.wireOp",EDGE,"E14.18.6"),sQuery(id+"F0.wireOp",EDGE,"E14.18.7"),sQuery(id+"F0.wireOp",EDGE,"E14.19.0"),sQuery(id+"F0.wireOp",EDGE,"E14.19.1"),sQuery(id+"F0.wireOp",EDGE,"E14.19.2"),sQuery(id+"F0.wireOp",EDGE,"E14.19.3"),sQuery(id+"F0.wireOp",EDGE,"E14.19.4"),sQuery(id+"F0.wireOp",EDGE,"E14.19.5"),sQuery(id+"F0.wireOp",EDGE,"E14.19.6"),sQuery(id+"F0.wireOp",EDGE,"E14.19.7"),sQuery(id+"F0.wireOp",EDGE,"E14.20.0"),sQuery(id+"F0.wireOp",EDGE,"E14.20.1"),sQuery(id+"F0.wireOp",EDGE,"E14.20.2"),sQuery(id+"F0.wireOp",EDGE,"E14.20.3"),sQuery(id+"F0.wireOp",EDGE,"E14.20.4"),sQuery(id+"F0.wireOp",EDGE,"E14.20.5"),sQuery(id+"F0.wireOp",EDGE,"E14.20.6"),sQuery(id+"F0.wireOp",EDGE,"E14.20.7"),sQuery(id+"F0.wireOp",EDGE,"E14.21.0"),sQuery(id+"F0.wireOp",EDGE,"E14.21.1"),sQuery(id+"F0.wireOp",EDGE,"E14.21.2"),sQuery(id+"F0.wireOp",EDGE,"E14.21.3"),sQuery(id+"F0.wireOp",EDGE,"E14.21.4"),sQuery(id+"F0.wireOp",EDGE,"E14.21.5"),sQuery(id+"F0.wireOp",EDGE,"E14.21.6"),sQuery(id+"F0.wireOp",EDGE,"E14.21.7"),sQuery(id+"F0.wireOp",EDGE,"E14.22.0"),sQuery(id+"F0.wireOp",EDGE,"E14.22.1"),sQuery(id+"F0.wireOp",EDGE,"E14.22.2"),sQuery(id+"F0.wireOp",EDGE,"E14.22.3"),sQuery(id+"F0.wireOp",EDGE,"E14.22.4"),sQuery(id+"F0.wireOp",EDGE,"E14.22.5"),sQuery(id+"F0.wireOp",EDGE,"E14.22.6"),sQuery(id+"F0.wireOp",EDGE,"E14.22.7"),sQuery(id+"F0.wireOp",EDGE,"E14.23.0"),sQuery(id+"F0.wireOp",EDGE,"E14.23.1"),sQuery(id+"F0.wireOp",EDGE,"E14.23.2"),sQuery(id+"F0.wireOp",EDGE,"E14.23.3"),sQuery(id+"F0.wireOp",EDGE,"E14.23.4"),sQuery(id+"F0.wireOp",EDGE,"E14.23.5"),sQuery(id+"F0.wireOp",EDGE,"E14.23.6"),sQuery(id+"F0.wireOp",EDGE,"E14.23.7"),sQuery(id+"F0.wireOp",EDGE,"E14.24.0"),sQuery(id+"F0.wireOp",EDGE,"E14.24.1"),sQuery(id+"F0.wireOp",EDGE,"E14.24.2"),sQuery(id+"F0.wireOp",EDGE,"E14.24.3"),sQuery(id+"F0.wireOp",EDGE,"E14.24.4"),sQuery(id+"F0.wireOp",EDGE,"E14.24.5"),sQuery(id+"F0.wireOp",EDGE,"E14.24.6"),sQuery(id+"F0.wireOp",EDGE,"E14.24.7"),sQuery(id+"F0.wireOp",EDGE,"E14.25.0"),sQuery(id+"F0.wireOp",EDGE,"E14.25.1"),sQuery(id+"F0.wireOp",EDGE,"E14.25.2"),sQuery(id+"F0.wireOp",EDGE,"E14.25.3"),sQuery(id+"F0.wireOp",EDGE,"E14.25.4"),sQuery(id+"F0.wireOp",EDGE,"E14.25.5"),sQuery(id+"F0.wireOp",EDGE,"E14.25.6"),sQuery(id+"F0.wireOp",EDGE,"E14.25.7"),sQuery(id+"F0.wireOp",EDGE,"E14.26.0"),sQuery(id+"F0.wireOp",EDGE,"E14.26.1"),sQuery(id+"F0.wireOp",EDGE,"E14.26.2"),sQuery(id+"F0.wireOp",EDGE,"E14.26.3"),sQuery(id+"F0.wireOp",EDGE,"E14.26.4"),sQuery(id+"F0.wireOp",EDGE,"E14.26.5"),sQuery(id+"F0.wireOp",EDGE,"E14.26.6"),sQuery(id+"F0.wireOp",EDGE,"E14.26.7"),sQuery(id+"F0.wireOp",EDGE,"E14.27.0"),sQuery(id+"F0.wireOp",EDGE,"E14.27.1"),sQuery(id+"F0.wireOp",EDGE,"E14.27.2"),sQuery(id+"F0.wireOp",EDGE,"E14.27.3"),sQuery(id+"F0.wireOp",EDGE,"E14.27.4"),sQuery(id+"F0.wireOp",EDGE,"E14.27.5"),sQuery(id+"F0.wireOp",EDGE,"E14.27.6"),sQuery(id+"F0.wireOp",EDGE,"E14.27.7"),sQuery(id+"F0.wireOp",EDGE,"E14.28.0"),sQuery(id+"F0.wireOp",EDGE,"E14.28.1"),sQuery(id+"F0.wireOp",EDGE,"E14.28.2"),sQuery(id+"F0.wireOp",EDGE,"E14.28.3"),sQuery(id+"F0.wireOp",EDGE,"E14.28.4"),sQuery(id+"F0.wireOp",EDGE,"E14.28.5"),sQuery(id+"F0.wireOp",EDGE,"E14.28.6"),sQuery(id+"F0.wireOp",EDGE,"E14.28.7"),sQuery(id+"F0.wireOp",EDGE,"E14.29.0"),sQuery(id+"F0.wireOp",EDGE,"E14.29.1"),sQuery(id+"F0.wireOp",EDGE,"E14.29.2"),sQuery(id+"F0.wireOp",EDGE,"E14.29.3"),sQuery(id+"F0.wireOp",EDGE,"E14.29.4"),sQuery(id+"F0.wireOp",EDGE,"E14.29.5"),sQuery(id+"F0.wireOp",EDGE,"E14.29.6"),sQuery(id+"F0.wireOp",EDGE,"E14.29.7"),sQuery(id+"F0.wireOp",EDGE,"E14.30.0"),sQuery(id+"F0.wireOp",EDGE,"E14.30.1"),sQuery(id+"F0.wireOp",EDGE,"E14.30.2"),sQuery(id+"F0.wireOp",EDGE,"E14.30.3"),sQuery(id+"F0.wireOp",EDGE,"E14.30.4"),sQuery(id+"F0.wireOp",EDGE,"E14.30.5"),sQuery(id+"F0.wireOp",EDGE,"E14.30.6"),sQuery(id+"F0.wireOp",EDGE,"E14.30.7"),sQuery(id+"F0.wireOp",EDGE,"E14.31.0"),sQuery(id+"F0.wireOp",EDGE,"E14.31.1"),sQuery(id+"F0.wireOp",EDGE,"E14.31.2"),sQuery(id+"F0.wireOp",EDGE,"E14.31.3"),sQuery(id+"F0.wireOp",EDGE,"E14.31.4"),sQuery(id+"F0.wireOp",EDGE,"E14.31.5"),sQuery(id+"F0.wireOp",EDGE,"E14.31.6"),sQuery(id+"F0.wireOp",EDGE,"E14.31.7"),sQuery(id+"F0.wireOp",EDGE,"E14.32.0"),sQuery(id+"F0.wireOp",EDGE,"E14.32.1"),sQuery(id+"F0.wireOp",EDGE,"E14.32.2"),sQuery(id+"F0.wireOp",EDGE,"E14.32.3"),sQuery(id+"F0.wireOp",EDGE,"E14.32.4"),sQuery(id+"F0.wireOp",EDGE,"E14.32.5"),sQuery(id+"F0.wireOp",EDGE,"E14.32.6"),sQuery(id+"F0.wireOp",EDGE,"E14.32.7"),sQuery(id+"F0.wireOp",EDGE,"E14.33.0"),sQuery(id+"F0.wireOp",EDGE,"E14.33.1"),sQuery(id+"F0.wireOp",EDGE,"E14.33.2"),sQuery(id+"F0.wireOp",EDGE,"E14.33.3"),sQuery(id+"F0.wireOp",EDGE,"E14.33.4"),sQuery(id+"F0.wireOp",EDGE,"E14.33.5"),sQuery(id+"F0.wireOp",EDGE,"E14.33.6"),sQuery(id+"F0.wireOp",EDGE,"E14.33.7"),sQuery(id+"F0.wireOp",EDGE,"E14.34.0"),sQuery(id+"F0.wireOp",EDGE,"E14.34.1"),sQuery(id+"F0.wireOp",EDGE,"E14.34.2"),sQuery(id+"F0.wireOp",EDGE,"E14.34.3"),sQuery(id+"F0.wireOp",EDGE,"E14.34.4"),sQuery(id+"F0.wireOp",EDGE,"E14.34.5"),sQuery(id+"F0.wireOp",EDGE,"E14.34.6"),sQuery(id+"F0.wireOp",EDGE,"E14.34.7"),sQuery(id+"F0.wireOp",EDGE,"E14.35.0"),sQuery(id+"F0.wireOp",EDGE,"E14.35.1"),sQuery(id+"F0.wireOp",EDGE,"E14.35.2"),sQuery(id+"F0.wireOp",EDGE,"E14.35.3"),sQuery(id+"F0.wireOp",EDGE,"E14.35.4"),sQuery(id+"F0.wireOp",EDGE,"E14.35.5"),sQuery(id+"F0.wireOp",EDGE,"E14.35.6"),sQuery(id+"F0.wireOp",EDGE,"E14.35.7"),sQuery(id+"F0.wireOp",EDGE,"E14.36.0"),sQuery(id+"F0.wireOp",EDGE,"E14.36.1"),sQuery(id+"F0.wireOp",EDGE,"E14.36.2"),sQuery(id+"F0.wireOp",EDGE,"E14.36.3"),sQuery(id+"F0.wireOp",EDGE,"E14.36.4"),sQuery(id+"F0.wireOp",EDGE,"E14.36.5"),sQuery(id+"F0.wireOp",EDGE,"E14.36.6"),sQuery(id+"F0.wireOp",EDGE,"E14.36.7"),sQuery(id+"F0.wireOp",EDGE,"E14.37.0"),sQuery(id+"F0.wireOp",EDGE,"E14.37.1"),sQuery(id+"F0.wireOp",EDGE,"E14.37.2"),sQuery(id+"F0.wireOp",EDGE,"E14.37.3"),sQuery(id+"F0.wireOp",EDGE,"E14.37.4"),sQuery(id+"F0.wireOp",EDGE,"E14.37.5"),sQuery(id+"F0.wireOp",EDGE,"E14.37.6"),sQuery(id+"F0.wireOp",EDGE,"E14.37.7"),sQuery(id+"F0.wireOp",EDGE,"E14.38.0"),sQuery(id+"F0.wireOp",EDGE,"E14.38.1"),sQuery(id+"F0.wireOp",EDGE,"E14.38.2"),sQuery(id+"F0.wireOp",EDGE,"E14.38.3"),sQuery(id+"F0.wireOp",EDGE,"E14.38.4"),sQuery(id+"F0.wireOp",EDGE,"E14.38.5"),sQuery(id+"F0.wireOp",EDGE,"E14.38.6"),sQuery(id+"F0.wireOp",EDGE,"E14.38.7"),sQuery(id+"F0.wireOp",EDGE,"E14.39.0"),sQuery(id+"F0.wireOp",EDGE,"E14.39.1"),sQuery(id+"F0.wireOp",EDGE,"E14.39.2"),sQuery(id+"F0.wireOp",EDGE,"E14.39.3"),sQuery(id+"F0.wireOp",EDGE,"E14.39.4"),sQuery(id+"F0.wireOp",EDGE,"E14.39.5"),sQuery(id+"F0.wireOp",EDGE,"E14.39.6"),sQuery(id+"F0.wireOp",EDGE,"E14.39.7"),sQuery(id+"F0.wireOp",EDGE,"E14.40.0"),sQuery(id+"F0.wireOp",EDGE,"E14.40.1"),sQuery(id+"F0.wireOp",EDGE,"E14.40.2"),sQuery(id+"F0.wireOp",EDGE,"E14.40.3"),sQuery(id+"F0.wireOp",EDGE,"E14.40.4"),sQuery(id+"F0.wireOp",EDGE,"E14.40.5"),sQuery(id+"F0.wireOp",EDGE,"E14.40.6"),sQuery(id+"F0.wireOp",EDGE,"E14.40.7"),sQuery(id+"F0.wireOp",EDGE,"E14.41.0"),sQuery(id+"F0.wireOp",EDGE,"E14.41.1"),sQuery(id+"F0.wireOp",EDGE,"E14.41.2"),sQuery(id+"F0.wireOp",EDGE,"E14.41.3"),sQuery(id+"F0.wireOp",EDGE,"E14.41.4"),sQuery(id+"F0.wireOp",EDGE,"E14.41.5"),sQuery(id+"F0.wireOp",EDGE,"E14.41.6"),sQuery(id+"F0.wireOp",EDGE,"E14.41.7"),sQuery(id+"F0.wireOp",EDGE,"E14.42.0"),sQuery(id+"F0.wireOp",EDGE,"E14.42.1"),sQuery(id+"F0.wireOp",EDGE,"E14.42.2"),sQuery(id+"F0.wireOp",EDGE,"E14.42.3"),sQuery(id+"F0.wireOp",EDGE,"E14.42.4"),sQuery(id+"F0.wireOp",EDGE,"E14.42.5"),sQuery(id+"F0.wireOp",EDGE,"E14.42.6"),sQuery(id+"F0.wireOp",EDGE,"E14.42.7"),sQuery(id+"F0.wireOp",EDGE,"E14.43.0"),sQuery(id+"F0.wireOp",EDGE,"E14.43.1"),sQuery(id+"F0.wireOp",EDGE,"E14.43.2"),sQuery(id+"F0.wireOp",EDGE,"E14.43.3"),sQuery(id+"F0.wireOp",EDGE,"E14.43.4"),sQuery(id+"F0.wireOp",EDGE,"E14.43.5"),sQuery(id+"F0.wireOp",EDGE,"E14.43.6"),sQuery(id+"F0.wireOp",EDGE,"E14.43.7"),sQuery(id+"F0.wireOp",EDGE,"E14.44.0"),sQuery(id+"F0.wireOp",EDGE,"E14.44.1"),sQuery(id+"F0.wireOp",EDGE,"E14.44.2"),sQuery(id+"F0.wireOp",EDGE,"E14.44.3"),sQuery(id+"F0.wireOp",EDGE,"E14.44.4"),sQuery(id+"F0.wireOp",EDGE,"E14.44.5"),sQuery(id+"F0.wireOp",EDGE,"E14.44.6"),sQuery(id+"F0.wireOp",EDGE,"E14.44.7"),sQuery(id+"F0.wireOp",EDGE,"E14.45.0"),sQuery(id+"F0.wireOp",EDGE,"E14.45.1"),sQuery(id+"F0.wireOp",EDGE,"E14.45.2"),sQuery(id+"F0.wireOp",EDGE,"E14.45.3"),sQuery(id+"F0.wireOp",EDGE,"E14.45.4"),sQuery(id+"F0.wireOp",EDGE,"E14.45.5"),sQuery(id+"F0.wireOp",EDGE,"E14.45.6"),sQuery(id+"F0.wireOp",EDGE,"E14.45.7"),sQuery(id+"F0.wireOp",EDGE,"E14.46.0"),sQuery(id+"F0.wireOp",EDGE,"E14.46.1"),sQuery(id+"F0.wireOp",EDGE,"E14.46.2"),sQuery(id+"F0.wireOp",EDGE,"E14.46.3"),sQuery(id+"F0.wireOp",EDGE,"E14.46.4"),sQuery(id+"F0.wireOp",EDGE,"E14.46.5"),sQuery(id+"F0.wireOp",EDGE,"E14.46.6"),sQuery(id+"F0.wireOp",EDGE,"E14.46.7"),sQuery(id+"F0.wireOp",EDGE,"E14.47.0"),sQuery(id+"F0.wireOp",EDGE,"E14.47.1"),sQuery(id+"F0.wireOp",EDGE,"E14.47.2"),sQuery(id+"F0.wireOp",EDGE,"E14.47.3"),sQuery(id+"F0.wireOp",EDGE,"E14.47.4"),sQuery(id+"F0.wireOp",EDGE,"E14.47.5"),sQuery(id+"F0.wireOp",EDGE,"E14.47.6"),sQuery(id+"F0.wireOp",EDGE,"E14.47.7")])],"isStart":false});
            var sketch = newSketch(context, id + "F8", { "sketchPlane" : qUnion([Q0])});
            skCircle(sketch, "E19", {"center": v(-0.16, 0.4) * mm, "radius": 22.5 * mm});
            skCircle(sketch, "E20", {"center": v(0, 0) * mm, "radius": 15 * mm});
            skSolve(sketch);
        }
        {
            var Q0;
            Q0=makeQuery(id+"F8.imprint","IMPRINT",FACE,{"disambiguationData":[TD([[makeQuery(id+"F8.imprint","IMPRINT",EDGE,{"derivedFrom":sQuery(id+"F8.wireOp",EDGE,"E19")}),1.0]])]});
            extrude(context, id + "F9", {"entities" : qUnion([Q0]), "operationType" : NewBodyOperationType.ADD, "oppositeDirection" : true, "depth" : 15 * mm});
        }
        {
            var Q0;
            Q0=makeQuery(id+"F5.boolean.opBoolean","COPY",FACE,{"derivedFrom":makeQuery(id+"F5.opExtrude","CAP_FACE",FACE,{"disambiguationData":[OSD([sQuery(id+"F2.wireOp",EDGE,"E16"),sQuery(id+"F4.wireOp",EDGE,"E17")])],"isStart":false})});
            var sketch = newSketch(context, id + "F10", { "sketchPlane" : qUnion([Q0])});
            skCircle(sketch, "E21", {"center": v(-40, 0) * mm, "radius": 9 * mm});
            skCircle(sketch, "E22.1.0", {"center": v(-33.65, -21.63) * mm, "radius": 9 * mm});
            skCircle(sketch, "E22.2.0", {"center": v(-16.62, -36.39) * mm, "radius": 9 * mm});
            skCircle(sketch, "E22.3.0", {"center": v(5.7, -39.6) * mm, "radius": 9 * mm});
            skCircle(sketch, "E22.4.0", {"center": v(26.2, -30.23) * mm, "radius": 9 * mm});
            skCircle(sketch, "E22.5.0", {"center": v(38.38, -11.27) * mm, "radius": 9 * mm});
            skCircle(sketch, "E22.6.0", {"center": v(38.38, 11.27) * mm, "radius": 9 * mm});
            skCircle(sketch, "E22.7.0", {"center": v(26.2, 30.23) * mm, "radius": 9 * mm});
            skCircle(sketch, "E22.8.0", {"center": v(5.7, 39.6) * mm, "radius": 9 * mm});
            skCircle(sketch, "E22.9.0", {"center": v(-16.62, 36.39) * mm, "radius": 9 * mm});
            skCircle(sketch, "E22.10.0", {"center": v(-33.65, 21.63) * mm, "radius": 9 * mm});
            skPoint(sketch, "E22.center", {"position": v(0, 0) * mm});
            skSolve(sketch);
        }
        {
            var Q0;
            Q0=makeQuery(id+"F10.imprint","IMPRINT",FACE,{"disambiguationData":[TD([[makeQuery(id+"F10.imprint","IMPRINT",EDGE,{"derivedFrom":sQuery(id+"F10.wireOp",EDGE,"E21")}),1.0]])]});
            var Q1;
            Q1=makeQuery(id+"F10.imprint","IMPRINT",FACE,{"disambiguationData":[TD([[makeQuery(id+"F10.imprint","IMPRINT",EDGE,{"derivedFrom":sQuery(id+"F10.wireOp",EDGE,"E22.10.0")}),1.0]])]});
            var Q2;
            Q2=makeQuery(id+"F10.imprint","IMPRINT",FACE,{"disambiguationData":[TD([[makeQuery(id+"F10.imprint","IMPRINT",EDGE,{"derivedFrom":sQuery(id+"F10.wireOp",EDGE,"E22.9.0")}),1.0]])]});
            var Q3;
            Q3=makeQuery(id+"F10.imprint","IMPRINT",FACE,{"disambiguationData":[TD([[makeQuery(id+"F10.imprint","IMPRINT",EDGE,{"derivedFrom":sQuery(id+"F10.wireOp",EDGE,"E22.8.0")}),1.0]])]});
            var Q4;
            Q4=makeQuery(id+"F10.imprint","IMPRINT",FACE,{"disambiguationData":[TD([[makeQuery(id+"F10.imprint","IMPRINT",EDGE,{"derivedFrom":sQuery(id+"F10.wireOp",EDGE,"E22.7.0")}),1.0]])]});
            var Q5;
            Q5=makeQuery(id+"F10.imprint","IMPRINT",FACE,{"disambiguationData":[TD([[makeQuery(id+"F10.imprint","IMPRINT",EDGE,{"derivedFrom":sQuery(id+"F10.wireOp",EDGE,"E22.6.0")}),1.0]])]});
            var Q6;
            Q6=makeQuery(id+"F10.imprint","IMPRINT",FACE,{"disambiguationData":[TD([[makeQuery(id+"F10.imprint","IMPRINT",EDGE,{"derivedFrom":sQuery(id+"F10.wireOp",EDGE,"E22.5.0")}),1.0]])]});
            var Q7;
            Q7=makeQuery(id+"F10.imprint","IMPRINT",FACE,{"disambiguationData":[TD([[makeQuery(id+"F10.imprint","IMPRINT",EDGE,{"derivedFrom":sQuery(id+"F10.wireOp",EDGE,"E22.4.0")}),1.0]])]});
            var Q8;
            Q8=makeQuery(id+"F10.imprint","IMPRINT",FACE,{"disambiguationData":[TD([[makeQuery(id+"F10.imprint","IMPRINT",EDGE,{"derivedFrom":sQuery(id+"F10.wireOp",EDGE,"E22.3.0")}),1.0]])]});
            var Q9;
            Q9=makeQuery(id+"F10.imprint","IMPRINT",FACE,{"disambiguationData":[TD([[makeQuery(id+"F10.imprint","IMPRINT",EDGE,{"derivedFrom":sQuery(id+"F10.wireOp",EDGE,"E22.1.0")}),1.0]])]});
            var Q10;
            Q10=makeQuery(id+"F10.imprint","IMPRINT",FACE,{"disambiguationData":[TD([[makeQuery(id+"F10.imprint","IMPRINT",EDGE,{"derivedFrom":sQuery(id+"F10.wireOp",EDGE,"E22.2.0")}),1.0]])]});
            extrude(context, id + "F11", {"entities" : qUnion([Q0, Q1, Q2, Q3, Q4, Q5, Q6, Q7, Q8, Q9, Q10]), "operationType" : NewBodyOperationType.REMOVE, "endBound" : BoundingType.UP_TO_NEXT, "oppositeDirection" : true, "depth" : 25 * mm});
        }
    });
